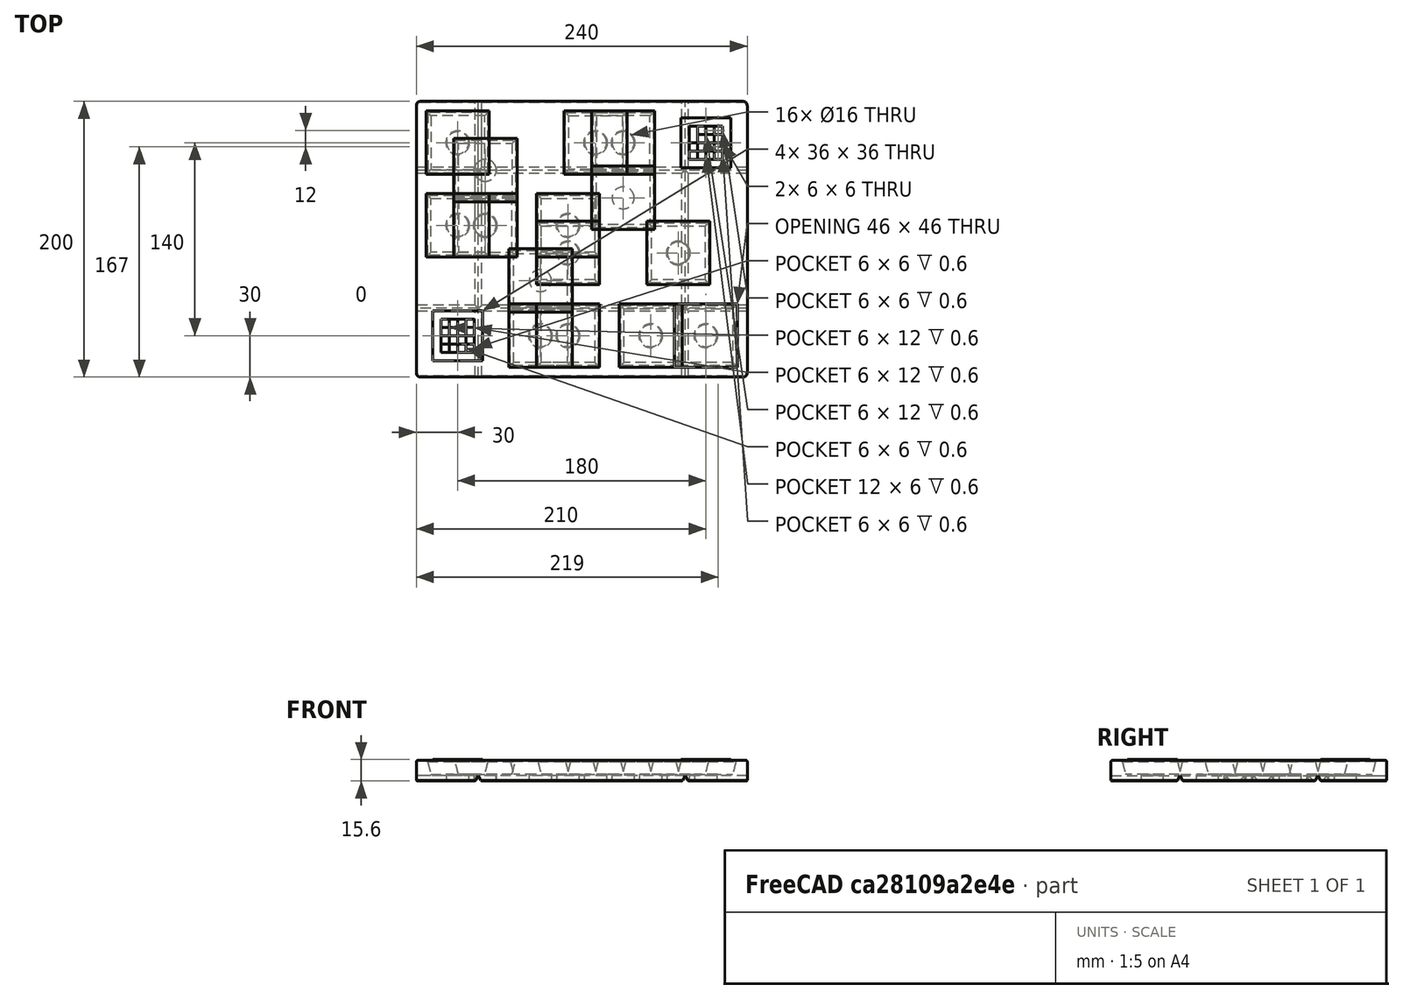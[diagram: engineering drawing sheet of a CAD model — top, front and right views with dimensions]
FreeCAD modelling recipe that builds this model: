
FCSTD DOCUMENT  (FreeCAD 0.21R33771 (Git))
Label: rob2024_plates
License: All rights reserved
LicenseURL: https://en.wikipedia.org/wiki/All_rights_reserved
objects: Sketcher::SketchObject×52, TechDraw::DrawViewDimension×44, PartDesign::SubtractiveLoft×16, PartDesign::Pocket×12, PartDesign::Chamfer×10, PartDesign::Pad×8, TechDraw::DrawGeomHatch×7, TechDraw::DrawSVGTemplate×4, PartDesign::Plane×4, PartDesign::Fillet×4, PartDesign::Body×4, TechDraw::DrawProjGroupItem×4, TechDraw::DrawProjGroup×4, TechDraw::DrawPage×4
note: 245 computed .brp shape members not serialized (recipe doc carries the construction recipe); baked Part::Feature solids carry a one-line shape summary decoded from their .brp

FEATURE [TechDraw::DrawSVGTemplate] Template
  Height = 297
  Orientation = 0
  Template = C:/Program Files/FreeCAD 0.21/data/Mod/TechDraw/Templates/A4_Portrait_blank.svg
  Width = 210
FEATURE [Sketcher::SketchObject] Sketch015
  FullyConstrained = true
  MapMode = 5
  Support = -> [XY_Plane001]
  sketch-geometry (16):
    g0: LineSegment StartX=-27 StartY=170 StartZ=0 EndX=207 EndY=170 EndZ=0
    g1: LineSegment StartX=210 StartY=167 StartZ=0 EndX=210 EndY=-27 EndZ=0
    g2: LineSegment StartX=207 StartY=-30 StartZ=0 EndX=-27 EndY=-30 EndZ=0
    g3: LineSegment StartX=-30 StartY=-27 StartZ=0 EndX=-30 EndY=167 EndZ=0
    g4: LineSegment StartX=-25 StartY=25 StartZ=0 EndX=25 EndY=25 EndZ=0
    g5: LineSegment StartX=25 StartY=25 StartZ=0 EndX=25 EndY=-25 EndZ=0
    g6: LineSegment StartX=25 StartY=-25 StartZ=0 EndX=-25 EndY=-25 EndZ=0
    g7: LineSegment StartX=-25 StartY=-25 StartZ=0 EndX=-25 EndY=25 EndZ=0
    g8: LineSegment StartX=155 StartY=165 StartZ=0 EndX=205 EndY=165 EndZ=0
    g9: LineSegment StartX=205 StartY=165 StartZ=0 EndX=205 EndY=115 EndZ=0
    g10: LineSegment StartX=205 StartY=115 StartZ=0 EndX=155 EndY=115 EndZ=0
    g11: LineSegment StartX=155 StartY=115 StartZ=0 EndX=155 EndY=165 EndZ=0
    g12: ArcOfCircle CenterX=-27 CenterY=-27 CenterZ=0 NormalX=0 NormalY=0 NormalZ=1 AngleXU=0 Radius=3 StartAngle=3.14159 EndAngle=4.71239
    g13: ArcOfCircle CenterX=207 CenterY=-27 CenterZ=0 NormalX=0 NormalY=0 NormalZ=1 AngleXU=0 Radius=3 StartAngle=4.71239 EndAngle=6.28319
    g14: ArcOfCircle CenterX=207 CenterY=167 CenterZ=0 NormalX=0 NormalY=0 NormalZ=1 AngleXU=0 Radius=3 StartAngle=1.7e-15 EndAngle=1.5708
    g15: ArcOfCircle CenterX=-27 CenterY=167 CenterZ=0 NormalX=0 NormalY=0 NormalZ=1 AngleXU=0 Radius=3 StartAngle=1.5708 EndAngle=3.14159
  constraints (44):
    c: Horizontal(g0)
    c: Horizontal(g2)
    c: Vertical(g1)
    c: Vertical(g3)
    c: Coincident(g4,g5)
    c: Coincident(g5,g6)
    c: Coincident(g6,g7)
    c: Coincident(g7,g4)
    c: Horizontal(g4)
    c: Horizontal(g6)
    c: Vertical(g5)
    c: Vertical(g7)
    c: DistanceY(g7,g7) = 50
    c: Coincident(g8,g9)
    c: Coincident(g9,g10)
    c: Coincident(g10,g11)
    c: Coincident(g11,g8)
    c: Horizontal(g8)
    c: Horizontal(g10)
    c: Vertical(g9)
    c: Vertical(g11)
    c: DistanceY(g9,g9) = 50
    c: DistanceX(g10,g10) = 50
    c: Distance(g9,g1) = 5
    c: Distance(g4,g3) = 5
    c: Distance(g6,g2) = 5
    c: Distance(g8,g0) = 5
    c: DistanceX(g6,g6) = 50
    c: Tangent(g2,g12) = 1.5708
    c: Tangent(g3,g12) = 1.5708
    c: Radius(g12) = 3
    c: Distance(g2,g0) = 200
    c: Tangent(g2,g13) = 1.5708
    c: Tangent(g1,g13) = 1.5708
    c: Tangent(g0,g14) = 1.5708
    c: Tangent(g1,g14) = 1.5708
    c: Tangent(g0,g15) = 1.5708
    c: Tangent(g3,g15) = 1.5708
    c: Equal(g12,g15)
    c: Equal(g12,g14)
    c: Equal(g12,g13)
    c: Distance(g3,g-2) = 30
    c: Distance(g2,g-1) = 30
    c: Distance(g3,g1) = 240
FEATURE [PartDesign::Pad] Pad002
  Direction = (0,0,1)
  Length = 15
  Length2 = 10
  Profile = -> Sketch015
  ReferenceAxis = -> Sketch015 [N_Axis]
  Reversed = true
  Type = 0
FEATURE [Sketcher::SketchObject] Sketch016  label="Sketch_rails_short_02"
  ExternalGeometry = -> [Pad002]
  FullyConstrained = true
  MapMode = 5
  Placement = pos=(210,0,0) rot=(0.57735,0.57735,0.57735;2.0944rad)
  Support = -> [Pad002]
  sketch-geometry (6):
    g0: LineSegment StartX=17.6906 StartY=-15 StartZ=0 EndX=20 EndY=-11 EndZ=0
    g1: LineSegment StartX=20 StartY=-11 StartZ=0 EndX=22.3094 EndY=-15 EndZ=0
    g2: LineSegment StartX=22.3094 StartY=-15 StartZ=0 EndX=17.6906 EndY=-15 EndZ=0
    g3: LineSegment StartX=117.691 StartY=-15 StartZ=0 EndX=120 EndY=-11 EndZ=0
    g4: LineSegment StartX=120 StartY=-11 StartZ=0 EndX=122.309 EndY=-15 EndZ=0
    g5: LineSegment StartX=122.309 StartY=-15 StartZ=0 EndX=117.691 EndY=-15 EndZ=0
  constraints (18):
    c: PointOnObject(g0,g-4)
    c: Coincident(g1,g0)
    c: PointOnObject(g1,g-4)
    c: Coincident(g2,g1)
    c: Coincident(g2,g0)
    c: Distance(g0,g2) = 4
    c: Angle(g0,g-2) = 0.523599
    c: Angle(g-2,g1) = 0.523599
    c: Coincident(g4,g3)
    c: Coincident(g5,g4)
    c: Coincident(g5,g3)
    c: Distance(g3,g5) = 4
    c: Angle(g3,g-2) = 0.523599
    c: Angle(g-2,g4) = 0.523599
    c: PointOnObject(g3,g-4)
    c: PointOnObject(g4,g-4)
    c: Distance(g0,g3) = 100
    c: Distance(g0,g-3) = 50
FEATURE [PartDesign::Pocket] Pocket003
  BaseFeature = -> Pad002
  Direction = (-1,0,0)
  Length = 5
  Length2 = 5
  Profile = -> Sketch016
  ReferenceAxis = -> Sketch016 [N_Axis]
  Type = 1
FEATURE [Sketcher::SketchObject] Sketch017  label="Sketch_rails_long_02"
  ExternalGeometry = -> [Pocket003]
  FullyConstrained = true
  MapMode = 5
  Placement = pos=(0,-30,0) rot=(1,0,0;1.5708rad)
  Support = -> [Pocket003]
  sketch-geometry (7):
    g0: LineSegment StartX=12.6906 StartY=-15 StartZ=0 EndX=15 EndY=-11 EndZ=0
    g1: LineSegment StartX=15 StartY=-11 StartZ=0 EndX=17.3094 EndY=-15 EndZ=0
    g2: LineSegment StartX=17.3094 StartY=-15 StartZ=0 EndX=12.6906 EndY=-15 EndZ=0
    g3: LineSegment StartX=162.691 StartY=-15 StartZ=0 EndX=165 EndY=-11 EndZ=0
    g4: LineSegment StartX=165 StartY=-11 StartZ=0 EndX=167.309 EndY=-15 EndZ=0
    g5: LineSegment StartX=167.309 StartY=-15 StartZ=0 EndX=162.691 EndY=-15 EndZ=0
    g6: LineSegment StartX=-30 StartY=-11 StartZ=0 EndX=210 EndY=-11 EndZ=0
  constraints (22):
    c: PointOnObject(g0,g-4)
    c: Coincident(g1,g0)
    c: PointOnObject(g1,g-4)
    c: Coincident(g2,g0)
    c: PointOnObject(g3,g-4)
    c: PointOnObject(g4,g-4)
    c: Coincident(g5,g3)
    c: Horizontal(g6)
    c: Distance(g-4,g6) = 4
    c: PointOnObject(g0,g6)
    c: PointOnObject(g3,g6)
    c: Coincident(g4,g3)
    c: DistanceX(g6,g6) = 240
    c: PointOnObject(g6,g-3)
    c: Angle(g0,g-2) = 0.523599
    c: Angle(g-2,g1) = 0.523599
    c: Angle(g3,g-2) = 0.523599
    c: Angle(g-2,g4) = 0.523599
    c: Coincident(g2,g1)
    c: Coincident(g5,g4)
    c: Distance(g0,g3) = 150
    c: Distance(g0,g-3) = 45
FEATURE [PartDesign::Pocket] Pocket004
  BaseFeature = -> Pocket003
  Direction = (0,1,-2e-16)
  Length = 5
  Length2 = 5
  Profile = -> Sketch017
  ReferenceAxis = -> Sketch017 [N_Axis]
  Type = 1
FEATURE [Sketcher::SketchObject] Sketch018
  ExternalGeometry = -> [Pocket004]
  FullyConstrained = true
  MapMode = 5
  Support = -> [Pocket004]
  sketch-geometry (42):
    g0: LineSegment StartX=-18 StartY=18 StartZ=0 EndX=18 EndY=18 EndZ=0
    g1: LineSegment StartX=18 StartY=18 StartZ=0 EndX=18 EndY=-18 EndZ=0
    g2: LineSegment StartX=18 StartY=-18 StartZ=0 EndX=-18 EndY=-18 EndZ=0
    g3: LineSegment StartX=-18 StartY=-18 StartZ=0 EndX=-18 EndY=18 EndZ=0
    g4: LineSegment StartX=180 StartY=170 StartZ=0 EndX=180 EndY=-30 EndZ=0
    g5: LineSegment StartX=-30 StartY=140 StartZ=0 EndX=210 EndY=140 EndZ=0
    g6: LineSegment StartX=162 StartY=158 StartZ=0 EndX=198 EndY=158 EndZ=0
    g7: LineSegment StartX=198 StartY=158 StartZ=0 EndX=198 EndY=122 EndZ=0
    g8: LineSegment StartX=198 StartY=122 StartZ=0 EndX=162 EndY=122 EndZ=0
    g9: LineSegment StartX=162 StartY=122 StartZ=0 EndX=162 EndY=158 EndZ=0
    g10: LineSegment StartX=-12 StartY=12 StartZ=0 EndX=-12 EndY=0 EndZ=0
    g11: LineSegment StartX=-12 StartY=0 StartZ=0 EndX=-6 EndY=0 EndZ=0
    g12: LineSegment StartX=-6 StartY=0 StartZ=0 EndX=-6 EndY=-12 EndZ=0
    g13: LineSegment StartX=-6 StartY=-12 StartZ=0 EndX=6 EndY=-12 EndZ=0
    g14: LineSegment StartX=6 StartY=-12 StartZ=0 EndX=6 EndY=-6 EndZ=0
    g15: LineSegment StartX=6 StartY=-6 StartZ=0 EndX=0 EndY=-6 EndZ=0
    g16: LineSegment StartX=0 StartY=0 StartZ=0 EndX=-6 EndY=1e-16 EndZ=0
    g17: LineSegment StartX=-6 StartY=1e-16 StartZ=0 EndX=-6 EndY=12 EndZ=0
    g18: LineSegment StartX=-6 StartY=12 StartZ=0 EndX=-12 EndY=12 EndZ=0
    g19: LineSegment StartX=6 StartY=12 StartZ=0 EndX=6 EndY=0 EndZ=0
    g20: LineSegment StartX=6 StartY=0 StartZ=0 EndX=12 EndY=1e-16 EndZ=0
    g21: LineSegment StartX=12 StartY=1e-16 StartZ=0 EndX=12 EndY=12 EndZ=0
    g22: LineSegment StartX=12 StartY=12 StartZ=0 EndX=6 EndY=12 EndZ=0
    g23: LineSegment StartX=0 StartY=-6 StartZ=0 EndX=0 EndY=0 EndZ=0
    g24: LineSegment StartX=168 StartY=128 StartZ=0 EndX=186 EndY=128 EndZ=0
    g25: LineSegment StartX=186 StartY=128 StartZ=0 EndX=186 EndY=134 EndZ=0
    g26: LineSegment StartX=186 StartY=134 StartZ=0 EndX=192 EndY=134 EndZ=0
    g27: LineSegment StartX=192 StartY=134 StartZ=0 EndX=192 EndY=140 EndZ=0
    g28: LineSegment StartX=192 StartY=140 StartZ=0 EndX=186 EndY=140 EndZ=0
    g29: LineSegment StartX=186 StartY=140 StartZ=0 EndX=186 EndY=134 EndZ=0
    g30: LineSegment StartX=186 StartY=134 StartZ=0 EndX=174 EndY=134 EndZ=0
    g31: LineSegment StartX=174 StartY=134 StartZ=0 EndX=174 EndY=140 EndZ=0
    g32: LineSegment StartX=174 StartY=140 StartZ=0 EndX=180 EndY=140 EndZ=0
    g33: LineSegment StartX=180 StartY=140 StartZ=0 EndX=180 EndY=152 EndZ=0
    g34: LineSegment StartX=180 StartY=152 StartZ=0 EndX=174 EndY=152 EndZ=0
    g35: LineSegment StartX=174 StartY=152 StartZ=0 EndX=174 EndY=140 EndZ=0
    g36: LineSegment StartX=174 StartY=140 StartZ=0 EndX=168 EndY=140 EndZ=0
    g37: LineSegment StartX=168 StartY=140 StartZ=0 EndX=168 EndY=128 EndZ=0
    g38: LineSegment StartX=186 StartY=152 StartZ=0 EndX=186 EndY=146 EndZ=0
    g39: LineSegment StartX=186 StartY=146 StartZ=0 EndX=192 EndY=146 EndZ=0
    g40: LineSegment StartX=192 StartY=146 StartZ=0 EndX=192 EndY=152 EndZ=0
    g41: LineSegment StartX=192 StartY=152 StartZ=0 EndX=186 EndY=152 EndZ=0
  constraints (113):
    c: Coincident(g0,g1)
    c: Coincident(g1,g2)
    c: Coincident(g2,g3)
    c: Coincident(g3,g0)
    c: Horizontal(g0)
    c: Vertical(g1)
    c: DistanceX(g2,g2) = 36
    c: Equal(g2,g1)
    c: Symmetric(g2,g1,g-2)
    c: Symmetric(g0,g2,g-1)
    c: Vertical(g4)
    c: Horizontal(g5)
    c: PointOnObject(g4,g-5)
    c: PointOnObject(g4,g-4)
    c: PointOnObject(g5,g-6)
    c: PointOnObject(g5,g-3)
    c: Distance(g5,g-1) = 140
    c: Distance(g4,g-2) = 180
    c: Coincident(g6,g7)
    c: Coincident(g7,g8)
    c: Coincident(g8,g9)
    c: Coincident(g9,g6)
    c: Horizontal(g6)
    c: Horizontal(g8)
    c: Vertical(g7)
    c: Vertical(g9)
    c: DistanceY(g7,g7) = 36
    c: Equal(g6,g7)
    c: Distance(g6,g5) = 18
    c: Distance(g6,g4) = 18
    c: Vertical(g10)
    c: Horizontal(g11)
    c: Vertical(g12)
    c: Coincident(g12,g13)
    c: Horizontal(g13)
    c: Vertical(g14)
    c: Coincident(g14,g15)
    c: Horizontal(g15)
    c: Coincident(g16,g17)
    c: Coincident(g18,g10)
    c: Horizontal(g18)
    c: Coincident(g19,g20)
    c: Vertical(g21)
    c: Coincident(g21,g22)
    c: Coincident(g22,g19)
    c: Coincident(g11,g10)
    c: Distance(g10,g3) = 6
    c: Distance(g12,g10) = 6
    c: Distance(g15,g12) = 6
    c: Distance(g15,g14) = 6
    c: Coincident(g11,g12)
    c: Coincident(g13,g14)
    c: Tangent(g11,g16)
    c: Coincident(g18,g17)
    c: Tangent(g19,g14)
    c: Coincident(g20,g21)
    c: DistanceX(g20,g20) = 6
    c: Tangent(g18,g22)
    c: Coincident(g23,g15)
    c: Coincident(g23,g16)
    c: Vertical(g23)
    c: Tangent(g11,g20)
    c: Tangent(g17,g12)
    c: Distance(g12,g2) = 6
    c: Distance(g15,g13) = 6
    c: Distance(g16,g15) = 6
    c: Distance(g17,g11) = 12
    c: Horizontal(g24)
    c: Coincident(g25,g24)
    c: Vertical(g25)
    c: Horizontal(g26)
    c: Vertical(g27)
    c: Horizontal(g28)
    c: Vertical(g31)
    c: Vertical(g33)
    c: Coincident(g34,g33)
    c: Horizontal(g34)
    c: Vertical(g37)
    c: Coincident(g24,g37)
    c: Coincident(g37,g36)
    c: Coincident(g39,g38)
    c: Horizontal(g39)
    c: Coincident(g41,g38)
    c: Distance(g24,g9) = 6
    c: Distance(g30,g37) = 6
    c: Distance(g32,g31) = 6
    c: Coincident(g31,g30)
    c: Coincident(g32,g31)
    c: Coincident(g33,g32)
    c: Tangent(g35,g31)
    c: Coincident(g34,g35)
    c: Coincident(g36,g35)
    c: Distance(g28,g33) = 6
    c: Coincident(g29,g30)
    c: Coincident(g29,g28)
    c: Tangent(g29,g25)
    c: Coincident(g26,g25)
    c: Distance(g27,g29) = 6
    c: Coincident(g28,g27)
    c: Coincident(g26,g27)
    c: Tangent(g41,g34)
    c: Tangent(g38,g29)
    c: Tangent(g40,g27)
    c: Coincident(g41,g40)
    c: Coincident(g39,g40)
    c: Tangent(g36,g32)
    c: Tangent(g30,g26)
    c: Tangent(g28,g32)
    c: Distance(g39,g28) = 6
    c: Distance(g40,g39) = 6
    c: Distance(g27,g26) = 6
    c: Distance(g26,g24) = 6
    c: Distance(g24,g8) = 6
FEATURE [PartDesign::Pad] Pad003
  BaseFeature = -> Pocket004
  Direction = (0,0,1)
  Length = 0.6
  Length2 = 10
  Profile = -> Sketch018
  ReferenceAxis = -> Sketch018 [N_Axis]
  Type = 0
FEATURE [Sketcher::SketchObject] Sketch019
  FullyConstrained = true
  MapMode = 5
  Support = -> [Pad003]
  sketch-geometry (4):
    g0: Circle CenterX=20 CenterY=120 CenterZ=0 NormalX=0 NormalY=0 NormalZ=1 AngleXU=0 Radius=8
    g1: Circle CenterX=120 CenterY=100 CenterZ=0 NormalX=0 NormalY=0 NormalZ=1 AngleXU=0 Radius=8
    g2: Circle CenterX=180 CenterY=0 CenterZ=0 NormalX=0 NormalY=0 NormalZ=1 AngleXU=0 Radius=8
    g3: Circle CenterX=60 CenterY=40 CenterZ=0 NormalX=0 NormalY=0 NormalZ=1 AngleXU=0 Radius=8
  constraints (12):
    c: Diameter(g0) = 16
    c: PointOnObject(g2,g-1)
    c: Distance(g2,g-2) = 180
    c: Equal(g2,g0)
    c: Distance(g3,g-1) = 40
    c: Distance(g3,g-2) = 60
    c: Equal(g3,g0)
    c: Distance(g1,g-2) = 120
    c: Distance(g1,g-1) = 100
    c: Equal(g0,g1)
    c: Distance(g0,g-1) = 120
    c: Distance(g0,g-2) = 20
FEATURE [PartDesign::Pocket] Pocket005
  BaseFeature = -> Pad003
  Direction = (0,0,-1)
  Length = 5
  Length2 = 5
  Profile = -> Sketch019
  ReferenceAxis = -> Sketch019 [N_Axis]
  Type = 1
FEATURE [PartDesign::Plane] DatumPlane001
  AttachmentOffset = pos=(0,0,-10) rot=(0,0,1;0rad)
  Length = 60
  MapMode = 5
  Placement = pos=(0,0,-10) rot=(0,0,1;0rad)
  ResizeMode = 0
  Support = -> [Pocket005]
  Width = 60
FEATURE [Sketcher::SketchObject] Sketch020
  ExternalGeometry = -> [Pocket005]
  FullyConstrained = true
  MapMode = 5
  Support = -> [Pocket005]
  sketch-geometry (4):
    g0: LineSegment StartX=38 StartY=62 StartZ=0 EndX=82 EndY=62 EndZ=0
    g1: LineSegment StartX=82 StartY=62 StartZ=0 EndX=82 EndY=18 EndZ=0
    g2: LineSegment StartX=82 StartY=18 StartZ=0 EndX=38 EndY=18 EndZ=0
    g3: LineSegment StartX=38 StartY=18 StartZ=0 EndX=38 EndY=62 EndZ=0
  constraints (11):
    c: Coincident(g0,g1)
    c: Coincident(g1,g2)
    c: Coincident(g2,g3)
    c: Coincident(g3,g0)
    c: Horizontal(g0)
    c: Horizontal(g2)
    c: Vertical(g1)
    c: Vertical(g3)
    c: DistanceY(g3,g3) = 44
    c: Equal(g3,g0)
    c: Symmetric(g0,g1,g-3)
FEATURE [Sketcher::SketchObject] Sketch021
  ExternalGeometry = -> [Pocket005]
  FullyConstrained = true
  MapMode = 5
  Placement = pos=(0,0,-10) rot=(0,0,1;0rad)
  Support = -> [DatumPlane001]
  sketch-geometry (4):
    g0: LineSegment StartX=40.5 StartY=59.5 StartZ=0 EndX=79.5 EndY=59.5 EndZ=0
    g1: LineSegment StartX=79.5 StartY=59.5 StartZ=0 EndX=79.5 EndY=20.5 EndZ=0
    g2: LineSegment StartX=79.5 StartY=20.5 StartZ=0 EndX=40.5 EndY=20.5 EndZ=0
    g3: LineSegment StartX=40.5 StartY=20.5 StartZ=0 EndX=40.5 EndY=59.5 EndZ=0
  constraints (11):
    c: Coincident(g0,g1)
    c: Coincident(g1,g2)
    c: Coincident(g2,g3)
    c: Coincident(g3,g0)
    c: Horizontal(g0)
    c: Horizontal(g2)
    c: Vertical(g1)
    c: Vertical(g3)
    c: DistanceY(g3,g3) = 39
    c: Equal(g3,g0)
    c: Symmetric(g0,g1,g-3)
FEATURE [Sketcher::SketchObject] Sketch022
  ExternalGeometry = -> [Pocket005]
  FullyConstrained = true
  MapMode = 5
  Support = -> [Pocket005]
  sketch-geometry (4):
    g0: LineSegment StartX=98 StartY=122 StartZ=0 EndX=142 EndY=122 EndZ=0
    g1: LineSegment StartX=142 StartY=122 StartZ=0 EndX=142 EndY=78 EndZ=0
    g2: LineSegment StartX=142 StartY=78 StartZ=0 EndX=98 EndY=78 EndZ=0
    g3: LineSegment StartX=98 StartY=78 StartZ=0 EndX=98 EndY=122 EndZ=0
  constraints (11):
    c: Coincident(g0,g1)
    c: Coincident(g1,g2)
    c: Coincident(g2,g3)
    c: Coincident(g3,g0)
    c: Horizontal(g0)
    c: Horizontal(g2)
    c: Vertical(g1)
    c: Vertical(g3)
    c: DistanceY(g3,g3) = 44
    c: Equal(g3,g0)
    c: Symmetric(g0,g1,g-3)
FEATURE [Sketcher::SketchObject] Sketch023
  ExternalGeometry = -> [Pocket005]
  FullyConstrained = true
  MapMode = 5
  Placement = pos=(0,0,-10) rot=(0,0,1;0rad)
  Support = -> [DatumPlane001]
  sketch-geometry (4):
    g0: LineSegment StartX=100.5 StartY=119.5 StartZ=0 EndX=139.5 EndY=119.5 EndZ=0
    g1: LineSegment StartX=139.5 StartY=119.5 StartZ=0 EndX=139.5 EndY=80.5 EndZ=0
    g2: LineSegment StartX=139.5 StartY=80.5 StartZ=0 EndX=100.5 EndY=80.5 EndZ=0
    g3: LineSegment StartX=100.5 StartY=80.5 StartZ=0 EndX=100.5 EndY=119.5 EndZ=0
  constraints (11):
    c: Coincident(g0,g1)
    c: Coincident(g1,g2)
    c: Coincident(g2,g3)
    c: Coincident(g3,g0)
    c: Horizontal(g0)
    c: Horizontal(g2)
    c: Vertical(g1)
    c: Vertical(g3)
    c: DistanceY(g3,g3) = 39
    c: Equal(g3,g0)
    c: Symmetric(g0,g1,g-3)
FEATURE [Sketcher::SketchObject] Sketch026
  ExternalGeometry = -> [Pocket005]
  FullyConstrained = true
  MapMode = 5
  Support = -> [Pocket005]
  sketch-geometry (4):
    g0: LineSegment StartX=-2 StartY=142 StartZ=0 EndX=42 EndY=142 EndZ=0
    g1: LineSegment StartX=42 StartY=142 StartZ=0 EndX=42 EndY=98 EndZ=0
    g2: LineSegment StartX=42 StartY=98 StartZ=0 EndX=-2 EndY=98 EndZ=0
    g3: LineSegment StartX=-2 StartY=98 StartZ=0 EndX=-2 EndY=142 EndZ=0
  constraints (11):
    c: Coincident(g0,g1)
    c: Coincident(g1,g2)
    c: Coincident(g2,g3)
    c: Coincident(g3,g0)
    c: Horizontal(g0)
    c: Horizontal(g2)
    c: Vertical(g1)
    c: Vertical(g3)
    c: DistanceY(g3,g3) = 44
    c: Equal(g3,g0)
    c: Symmetric(g0,g1,g-3)
FEATURE [Sketcher::SketchObject] Sketch027
  ExternalGeometry = -> [Pocket005]
  FullyConstrained = true
  MapMode = 5
  Placement = pos=(0,0,-10) rot=(0,0,1;0rad)
  Support = -> [DatumPlane001]
  sketch-geometry (4):
    g0: LineSegment StartX=0.5 StartY=139.5 StartZ=0 EndX=39.5 EndY=139.5 EndZ=0
    g1: LineSegment StartX=39.5 StartY=139.5 StartZ=0 EndX=39.5 EndY=100.5 EndZ=0
    g2: LineSegment StartX=39.5 StartY=100.5 StartZ=0 EndX=0.5 EndY=100.5 EndZ=0
    g3: LineSegment StartX=0.5 StartY=100.5 StartZ=0 EndX=0.5 EndY=139.5 EndZ=0
  constraints (11):
    c: Coincident(g0,g1)
    c: Coincident(g1,g2)
    c: Coincident(g2,g3)
    c: Coincident(g3,g0)
    c: Horizontal(g0)
    c: Horizontal(g2)
    c: Vertical(g1)
    c: Vertical(g3)
    c: DistanceY(g3,g3) = 39
    c: Equal(g0,g3)
    c: Symmetric(g0,g1,g-3)
FEATURE [PartDesign::SubtractiveLoft] SubtractiveLoft004
  BaseFeature = -> Pocket005
  Closed = false
  Profile = -> Sketch027
  Ruled = false
  Sections = -> [Sketch026]
FEATURE [PartDesign::SubtractiveLoft] SubtractiveLoft005
  BaseFeature = -> SubtractiveLoft004
  Closed = false
  Profile = -> Sketch020
  Ruled = false
  Sections = -> [Sketch021]
FEATURE [PartDesign::SubtractiveLoft] SubtractiveLoft006
  BaseFeature = -> SubtractiveLoft005
  Closed = false
  Profile = -> Sketch022
  Ruled = false
  Sections = -> [Sketch023]
FEATURE [Sketcher::SketchObject] Sketch024
  ExternalGeometry = -> [SubtractiveLoft006]
  FullyConstrained = true
  MapMode = 5
  Support = -> [SubtractiveLoft006]
  sketch-geometry (4):
    g0: LineSegment StartX=158 StartY=22 StartZ=0 EndX=202 EndY=22 EndZ=0
    g1: LineSegment StartX=202 StartY=22 StartZ=0 EndX=202 EndY=-22 EndZ=0
    g2: LineSegment StartX=202 StartY=-22 StartZ=0 EndX=158 EndY=-22 EndZ=0
    g3: LineSegment StartX=158 StartY=-22 StartZ=0 EndX=158 EndY=22 EndZ=0
  constraints (11):
    c: Coincident(g0,g1)
    c: Coincident(g1,g2)
    c: Coincident(g2,g3)
    c: Coincident(g3,g0)
    c: Horizontal(g0)
    c: Horizontal(g2)
    c: Vertical(g1)
    c: Vertical(g3)
    c: DistanceY(g3,g3) = 44
    c: Equal(g3,g0)
    c: Symmetric(g0,g1,g-3)
FEATURE [Sketcher::SketchObject] Sketch025
  ExternalGeometry = -> [SubtractiveLoft006]
  FullyConstrained = true
  MapMode = 5
  Placement = pos=(0,0,-10) rot=(0,0,1;0rad)
  Support = -> [DatumPlane001]
  sketch-geometry (4):
    g0: LineSegment StartX=160.5 StartY=19.5 StartZ=0 EndX=199.5 EndY=19.5 EndZ=0
    g1: LineSegment StartX=199.5 StartY=19.5 StartZ=0 EndX=199.5 EndY=-19.5 EndZ=0
    g2: LineSegment StartX=199.5 StartY=-19.5 StartZ=0 EndX=160.5 EndY=-19.5 EndZ=0
    g3: LineSegment StartX=160.5 StartY=-19.5 StartZ=0 EndX=160.5 EndY=19.5 EndZ=0
  constraints (11):
    c: Coincident(g0,g1)
    c: Coincident(g1,g2)
    c: Coincident(g2,g3)
    c: Coincident(g3,g0)
    c: Horizontal(g0)
    c: Horizontal(g2)
    c: Vertical(g1)
    c: Vertical(g3)
    c: DistanceY(g3,g3) = 39
    c: Equal(g3,g0)
    c: Symmetric(g0,g1,g-3)
FEATURE [PartDesign::SubtractiveLoft] SubtractiveLoft007
  BaseFeature = -> SubtractiveLoft006
  Closed = false
  Profile = -> Sketch024
  Ruled = false
  Sections = -> [Sketch025]
FEATURE [PartDesign::Chamfer] Chamfer002
  Angle = 45
  Base = -> SubtractiveLoft007 [Edge30,Edge32,Edge33,Edge31,Edge22,Edge24,Edge23,Edge25,Edge37,Edge36,Edge34,Edge35,Edge29,Edge28,Edge26,Edge27]
  BaseFeature = -> SubtractiveLoft007
  ChamferType = 0
  FlipDirection = false
  Size = 1
  Size2 = 1
  SupportTransform = false
  UseAllEdges = false
FEATURE [PartDesign::Fillet] Fillet001
  Base = -> Chamfer002 [Edge9]
  BaseFeature = -> Chamfer002
  Radius = 1
  SupportTransform = false
  UseAllEdges = false
FEATURE [Sketcher::SketchObject] Sketch
  FullyConstrained = true
  MapMode = 5
  Support = -> [XY_Plane]
  sketch-geometry (16):
    g0: LineSegment StartX=-27 StartY=170 StartZ=0 EndX=207 EndY=170 EndZ=0
    g1: LineSegment StartX=210 StartY=167 StartZ=0 EndX=210 EndY=-27 EndZ=0
    g2: LineSegment StartX=207 StartY=-30 StartZ=0 EndX=-27 EndY=-30 EndZ=0
    g3: LineSegment StartX=-30 StartY=-27 StartZ=0 EndX=-30 EndY=167 EndZ=0
    g4: LineSegment StartX=-25 StartY=25 StartZ=0 EndX=25 EndY=25 EndZ=0
    g5: LineSegment StartX=25 StartY=25 StartZ=0 EndX=25 EndY=-25 EndZ=0
    g6: LineSegment StartX=25 StartY=-25 StartZ=0 EndX=-25 EndY=-25 EndZ=0
    g7: LineSegment StartX=-25 StartY=-25 StartZ=0 EndX=-25 EndY=25 EndZ=0
    g8: LineSegment StartX=155 StartY=165 StartZ=0 EndX=205 EndY=165 EndZ=0
    g9: LineSegment StartX=205 StartY=165 StartZ=0 EndX=205 EndY=115 EndZ=0
    g10: LineSegment StartX=205 StartY=115 StartZ=0 EndX=155 EndY=115 EndZ=0
    g11: LineSegment StartX=155 StartY=115 StartZ=0 EndX=155 EndY=165 EndZ=0
    g12: ArcOfCircle CenterX=-27 CenterY=-27 CenterZ=0 NormalX=0 NormalY=0 NormalZ=1 AngleXU=0 Radius=3 StartAngle=3.14159 EndAngle=4.71239
    g13: ArcOfCircle CenterX=207 CenterY=-27 CenterZ=0 NormalX=0 NormalY=0 NormalZ=1 AngleXU=0 Radius=3 StartAngle=4.71239 EndAngle=6.28319
    g14: ArcOfCircle CenterX=207 CenterY=167 CenterZ=0 NormalX=0 NormalY=0 NormalZ=1 AngleXU=0 Radius=3 StartAngle=1.7e-15 EndAngle=1.5708
    g15: ArcOfCircle CenterX=-27 CenterY=167 CenterZ=0 NormalX=0 NormalY=0 NormalZ=1 AngleXU=0 Radius=3 StartAngle=1.5708 EndAngle=3.14159
  constraints (44):
    c: Horizontal(g0)
    c: Horizontal(g2)
    c: Vertical(g1)
    c: Vertical(g3)
    c: Coincident(g4,g5)
    c: Coincident(g5,g6)
    c: Coincident(g6,g7)
    c: Coincident(g7,g4)
    c: Horizontal(g4)
    c: Horizontal(g6)
    c: Vertical(g5)
    c: Vertical(g7)
    c: DistanceY(g7,g7) = 50
    c: Coincident(g8,g9)
    c: Coincident(g9,g10)
    c: Coincident(g10,g11)
    c: Coincident(g11,g8)
    c: Horizontal(g8)
    c: Horizontal(g10)
    c: Vertical(g9)
    c: Vertical(g11)
    c: DistanceY(g9,g9) = 50
    c: DistanceX(g10,g10) = 50
    c: Distance(g9,g1) = 5
    c: Distance(g4,g3) = 5
    c: Distance(g6,g2) = 5
    c: Distance(g8,g0) = 5
    c: DistanceX(g6,g6) = 50
    c: Tangent(g2,g12) = 1.5708
    c: Tangent(g3,g12) = 1.5708
    c: Radius(g12) = 3
    c: Distance(g2,g0) = 200
    c: Tangent(g2,g13) = 1.5708
    c: Tangent(g1,g13) = 1.5708
    c: Tangent(g0,g14) = 1.5708
    c: Tangent(g1,g14) = 1.5708
    c: Tangent(g0,g15) = 1.5708
    c: Tangent(g3,g15) = 1.5708
    c: Equal(g12,g15)
    c: Equal(g12,g14)
    c: Equal(g12,g13)
    c: Distance(g3,g-2) = 30
    c: Distance(g2,g-1) = 30
    c: Distance(g3,g1) = 240
FEATURE [PartDesign::Pad] Pad
  Direction = (0,0,1)
  Length = 15
  Length2 = 10
  Profile = -> Sketch
  ReferenceAxis = -> Sketch [N_Axis]
  Reversed = true
  Type = 0
FEATURE [Sketcher::SketchObject] Sketch001  label="Sketch_rails_short"
  ExternalGeometry = -> [Pad]
  FullyConstrained = true
  MapMode = 5
  Placement = pos=(210,0,0) rot=(0.57735,0.57735,0.57735;2.0944rad)
  Support = -> [Pad]
  sketch-geometry (6):
    g0: LineSegment StartX=17.6906 StartY=-15 StartZ=0 EndX=20 EndY=-11 EndZ=0
    g1: LineSegment StartX=20 StartY=-11 StartZ=0 EndX=22.3094 EndY=-15 EndZ=0
    g2: LineSegment StartX=22.3094 StartY=-15 StartZ=0 EndX=17.6906 EndY=-15 EndZ=0
    g3: LineSegment StartX=117.691 StartY=-15 StartZ=0 EndX=120 EndY=-11 EndZ=0
    g4: LineSegment StartX=120 StartY=-11 StartZ=0 EndX=122.309 EndY=-15 EndZ=0
    g5: LineSegment StartX=122.309 StartY=-15 StartZ=0 EndX=117.691 EndY=-15 EndZ=0
  constraints (18):
    c: PointOnObject(g0,g-4)
    c: Coincident(g1,g0)
    c: PointOnObject(g1,g-4)
    c: Coincident(g2,g1)
    c: Coincident(g2,g0)
    c: Distance(g0,g2) = 4
    c: Angle(g0,g-2) = 0.523599
    c: Angle(g-2,g1) = 0.523599
    c: Coincident(g4,g3)
    c: Coincident(g5,g4)
    c: Coincident(g5,g3)
    c: Distance(g3,g5) = 4
    c: Angle(g3,g-2) = 0.523599
    c: Angle(g-2,g4) = 0.523599
    c: PointOnObject(g3,g-4)
    c: PointOnObject(g4,g-4)
    c: Distance(g0,g3) = 100
    c: Distance(g0,g-3) = 50
FEATURE [PartDesign::Pocket] Pocket
  BaseFeature = -> Pad
  Direction = (-1,0,0)
  Length = 5
  Length2 = 5
  Profile = -> Sketch001
  ReferenceAxis = -> Sketch001 [N_Axis]
  Type = 1
FEATURE [Sketcher::SketchObject] Sketch002
  ExternalGeometry = -> [Pocket]
  FullyConstrained = true
  MapMode = 5
  Placement = pos=(0,-30,0) rot=(1,0,0;1.5708rad)
  Support = -> [Pocket]
  sketch-geometry (7):
    g0: LineSegment StartX=12.6906 StartY=-15 StartZ=0 EndX=15 EndY=-11 EndZ=0
    g1: LineSegment StartX=15 StartY=-11 StartZ=0 EndX=17.3094 EndY=-15 EndZ=0
    g2: LineSegment StartX=17.3094 StartY=-15 StartZ=0 EndX=12.6906 EndY=-15 EndZ=0
    g3: LineSegment StartX=162.691 StartY=-15 StartZ=0 EndX=165 EndY=-11 EndZ=0
    g4: LineSegment StartX=165 StartY=-11 StartZ=0 EndX=167.309 EndY=-15 EndZ=0
    g5: LineSegment StartX=167.309 StartY=-15 StartZ=0 EndX=162.691 EndY=-15 EndZ=0
    g6: LineSegment StartX=-30 StartY=-11 StartZ=0 EndX=210 EndY=-11 EndZ=0
  constraints (22):
    c: PointOnObject(g0,g-4)
    c: Coincident(g1,g0)
    c: PointOnObject(g1,g-4)
    c: Coincident(g2,g0)
    c: PointOnObject(g3,g-4)
    c: PointOnObject(g4,g-4)
    c: Coincident(g5,g3)
    c: Horizontal(g6)
    c: Distance(g-4,g6) = 4
    c: PointOnObject(g0,g6)
    c: PointOnObject(g3,g6)
    c: Coincident(g4,g3)
    c: DistanceX(g6,g6) = 240
    c: PointOnObject(g6,g-3)
    c: Angle(g0,g-2) = 0.523599
    c: Angle(g-2,g1) = 0.523599
    c: Angle(g3,g-2) = 0.523599
    c: Angle(g-2,g4) = 0.523599
    c: Coincident(g2,g1)
    c: Coincident(g5,g4)
    c: Distance(g0,g3) = 150
    c: Distance(g0,g-3) = 45
FEATURE [PartDesign::Pocket] Pocket001
  BaseFeature = -> Pocket
  Direction = (0,1,-2e-16)
  Length = 5
  Length2 = 5
  Profile = -> Sketch002
  ReferenceAxis = -> Sketch002 [N_Axis]
  Type = 1
FEATURE [Sketcher::SketchObject] Sketch003
  ExternalGeometry = -> [Pocket001]
  FullyConstrained = true
  MapMode = 5
  Support = -> [Pocket001]
  sketch-geometry (36):
    g0: LineSegment StartX=-18 StartY=18 StartZ=0 EndX=18 EndY=18 EndZ=0
    g1: LineSegment StartX=18 StartY=18 StartZ=0 EndX=18 EndY=-18 EndZ=0
    g2: LineSegment StartX=18 StartY=-18 StartZ=0 EndX=-18 EndY=-18 EndZ=0
    g3: LineSegment StartX=-18 StartY=-18 StartZ=0 EndX=-18 EndY=18 EndZ=0
    g4: LineSegment StartX=-12 StartY=-12 StartZ=0 EndX=-12 EndY=6 EndZ=0
    g5: LineSegment StartX=-12 StartY=6 StartZ=0 EndX=12 EndY=6 EndZ=0
    g6: LineSegment StartX=12 StartY=6 StartZ=0 EndX=12 EndY=-6 EndZ=0
    g7: LineSegment StartX=12 StartY=-6 StartZ=0 EndX=6 EndY=-6 EndZ=0
    g8: LineSegment StartX=6 StartY=-6 StartZ=0 EndX=6 EndY=-12 EndZ=0
    g9: LineSegment StartX=6 StartY=-12 StartZ=0 EndX=9e-16 EndY=-12 EndZ=0
    g10: LineSegment StartX=9e-16 StartY=-12 StartZ=0 EndX=9e-16 EndY=-6 EndZ=0
    g11: LineSegment StartX=9e-16 StartY=-6 StartZ=0 EndX=6 EndY=-6 EndZ=0
    g12: LineSegment StartX=6 StartY=-6 StartZ=0 EndX=6 EndY=9e-16 EndZ=0
    g13: LineSegment StartX=6 StartY=9e-16 StartZ=0 EndX=-6 EndY=9e-16 EndZ=0
    g14: LineSegment StartX=-6 StartY=9e-16 StartZ=0 EndX=-6 EndY=-12 EndZ=0
    g15: LineSegment StartX=-6 StartY=-12 StartZ=0 EndX=-12 EndY=-12 EndZ=0
    g16: LineSegment StartX=180 StartY=170 StartZ=0 EndX=180 EndY=-30 EndZ=0
    g17: LineSegment StartX=-30 StartY=140 StartZ=0 EndX=210 EndY=140 EndZ=0
    g18: LineSegment StartX=162 StartY=158 StartZ=0 EndX=198 EndY=158 EndZ=0
    g19: LineSegment StartX=198 StartY=158 StartZ=0 EndX=198 EndY=122 EndZ=0
    g20: LineSegment StartX=198 StartY=122 StartZ=0 EndX=162 EndY=122 EndZ=0
    g21: LineSegment StartX=162 StartY=122 StartZ=0 EndX=162 EndY=158 EndZ=0
    g22: LineSegment StartX=180 StartY=128 StartZ=0 EndX=168 EndY=128 EndZ=0
    g23: LineSegment StartX=168 StartY=128 StartZ=0 EndX=168 EndY=134 EndZ=0
    g24: LineSegment StartX=168 StartY=134 StartZ=0 EndX=180 EndY=134 EndZ=0
    g25: LineSegment StartX=180 StartY=134 StartZ=0 EndX=180 EndY=152 EndZ=0
    g26: LineSegment StartX=180 StartY=152 StartZ=0 EndX=192 EndY=152 EndZ=0
    g27: LineSegment StartX=192 StartY=152 StartZ=0 EndX=192 EndY=140 EndZ=0
    g28: LineSegment StartX=192 StartY=140 StartZ=0 EndX=186 EndY=140 EndZ=0
    g29: LineSegment StartX=186 StartY=140 StartZ=0 EndX=186 EndY=134 EndZ=0
    g30: LineSegment StartX=186 StartY=134 StartZ=0 EndX=192 EndY=134 EndZ=0
    g31: LineSegment StartX=192 StartY=134 StartZ=0 EndX=192 EndY=128 EndZ=0
    g32: LineSegment StartX=192 StartY=128 StartZ=0 EndX=186 EndY=128 EndZ=0
    g33: LineSegment StartX=186 StartY=128 StartZ=0 EndX=186 EndY=134 EndZ=0
    g34: LineSegment StartX=186 StartY=134 StartZ=0 EndX=180 EndY=134 EndZ=0
    g35: LineSegment StartX=180 StartY=134 StartZ=0 EndX=180 EndY=128 EndZ=0
  constraints (108):
    c: Coincident(g0,g1)
    c: Coincident(g1,g2)
    c: Coincident(g2,g3)
    c: Coincident(g3,g0)
    c: Horizontal(g0)
    c: Vertical(g1)
    c: DistanceX(g2,g2) = 36
    c: Equal(g2,g1)
    c: Symmetric(g2,g1,g-2)
    c: Symmetric(g0,g2,g-1)
    c: Vertical(g4)
    c: Coincident(g5,g6)
    c: Coincident(g6,g7)
    c: Coincident(g7,g8)
    c: Coincident(g8,g9)
    c: Coincident(g10,g11)
    c: Horizontal(g11)
    c: Coincident(g11,g12)
    c: Vertical(g12)
    c: Horizontal(g13)
    c: Coincident(g13,g14)
    c: Vertical(g14)
    c: Coincident(g15,g4)
    c: Horizontal(g15)
    c: Coincident(g15,g14)
    c: Coincident(g10,g9)
    c: Coincident(g13,g12)
    c: Coincident(g5,g4)
    c: Horizontal(g5)
    c: Horizontal(g7)
    c: Horizontal(g9)
    c: Vertical(g10)
    c: Vertical(g8)
    c: Vertical(g6)
    c: Distance(g4,g3) = 6
    c: DistanceX(g15,g15) = 6
    c: DistanceX(g7,g7) = 6
    c: DistanceX(g9,g9) = 6
    c: Equal(g9,g11)
    c: Distance(g14,g10) = 6
    c: Distance(g4,g2) = 6
    c: DistanceY(g10,g10) = 6
    c: Equal(g10,g8)
    c: DistanceY(g12,g12) = 6
    c: Distance(g13,g5) = 6
    c: Distance(g8,g2) = 6
    c: Vertical(g16)
    c: Horizontal(g17)
    c: PointOnObject(g16,g-5)
    c: PointOnObject(g16,g-4)
    c: PointOnObject(g17,g-6)
    c: PointOnObject(g17,g-3)
    c: Distance(g17,g-1) = 140
    c: Distance(g16,g-2) = 180
    c: Coincident(g18,g19)
    c: Coincident(g19,g20)
    c: Coincident(g20,g21)
    c: Coincident(g21,g18)
    c: Horizontal(g18)
    c: Horizontal(g20)
    c: Vertical(g19)
    c: Vertical(g21)
    c: DistanceY(g19,g19) = 36
    c: Equal(g18,g19)
    c: Distance(g18,g17) = 18
    c: Distance(g18,g16) = 18
    c: Horizontal(g22)
    c: Coincident(g22,g23)
    c: Coincident(g23,g24)
    c: Horizontal(g24)
    c: Coincident(g24,g25)
    c: Coincident(g25,g26)
    c: Horizontal(g26)
    c: Coincident(g26,g27)
    c: Vertical(g27)
    c: Horizontal(g28)
    c: Vertical(g29)
    c: Coincident(g29,g30)
    c: Coincident(g30,g31)
    c: Coincident(g31,g32)
    c: Horizontal(g32)
    c: Vertical(g33)
    c: Coincident(g33,g34)
    c: Coincident(g34,g35)
    c: Coincident(g35,g22)
    c: Vertical(g23)
    c: Vertical(g31)
    c: Horizontal(g30)
    c: Horizontal(g34)
    c: Vertical(g25)
    c: Vertical(g35)
    c: Distance(g22,g21) = 6
    c: DistanceX(g22,g22) = 12
    c: DistanceX(g32,g32) = 6
    c: DistanceX(g34,g34) = 6
    c: Equal(g32,g30)
    c: Equal(g22,g24)
    c: Equal(g32,g28)
    c: Coincident(g27,g28)
    c: Distance(g31,g20) = 6
    c: Coincident(g32,g33)
    c: Distance(g22,g20) = 6
    c: DistanceY(g31,g31) = 6
    c: DistanceY(g29,g29) = 6
    c: Coincident(g28,g29)
    c: DistanceY(g27,g27) = 12
    c: Equal(g31,g33)
    c: Equal(g31,g23)
FEATURE [PartDesign::Pad] Pad001
  BaseFeature = -> Pocket001
  Direction = (0,0,1)
  Length = 0.6
  Length2 = 10
  Profile = -> Sketch003
  ReferenceAxis = -> Sketch003 [N_Axis]
  Type = 0
FEATURE [Sketcher::SketchObject] Sketch004
  FullyConstrained = true
  MapMode = 5
  Support = -> [Pad001]
  sketch-geometry (4):
    g0: Circle CenterX=0 CenterY=80 CenterZ=0 NormalX=0 NormalY=0 NormalZ=1 AngleXU=0 Radius=8
    g1: Circle CenterX=100 CenterY=140 CenterZ=0 NormalX=0 NormalY=0 NormalZ=1 AngleXU=0 Radius=8
    g2: Circle CenterX=140 CenterY=0 CenterZ=0 NormalX=0 NormalY=0 NormalZ=1 AngleXU=0 Radius=8
    g3: Circle CenterX=80 CenterY=60 CenterZ=0 NormalX=0 NormalY=0 NormalZ=1 AngleXU=0 Radius=8
  constraints (12):
    c: PointOnObject(g0,g-2)
    c: Diameter(g0) = 16
    c: Distance(g0,g-1) = 80
    c: PointOnObject(g2,g-1)
    c: Distance(g2,g-2) = 140
    c: Equal(g2,g0)
    c: Distance(g3,g-1) = 60
    c: Distance(g3,g-2) = 80
    c: Equal(g3,g0)
    c: Distance(g1,g-2) = 100
    c: Distance(g1,g-1) = 140
    c: Equal(g0,g1)
FEATURE [PartDesign::Pocket] Pocket002
  BaseFeature = -> Pad001
  Direction = (0,0,-1)
  Length = 5
  Length2 = 5
  Profile = -> Sketch004
  ReferenceAxis = -> Sketch004 [N_Axis]
  Type = 1
FEATURE [PartDesign::Plane] DatumPlane
  AttachmentOffset = pos=(0,0,-10) rot=(0,0,1;0rad)
  Length = 60
  MapMode = 5
  Placement = pos=(0,0,-10) rot=(0,0,1;0rad)
  ResizeMode = 0
  Support = -> [Pocket002]
  Width = 60
FEATURE [Sketcher::SketchObject] Sketch007
  ExternalGeometry = -> [Pocket002]
  FullyConstrained = true
  MapMode = 5
  Support = -> [Pocket002]
  sketch-geometry (4):
    g0: LineSegment StartX=58 StartY=82 StartZ=0 EndX=102 EndY=82 EndZ=0
    g1: LineSegment StartX=102 StartY=82 StartZ=0 EndX=102 EndY=38 EndZ=0
    g2: LineSegment StartX=102 StartY=38 StartZ=0 EndX=58 EndY=38 EndZ=0
    g3: LineSegment StartX=58 StartY=38 StartZ=0 EndX=58 EndY=82 EndZ=0
  constraints (11):
    c: Coincident(g0,g1)
    c: Coincident(g1,g2)
    c: Coincident(g2,g3)
    c: Coincident(g3,g0)
    c: Horizontal(g0)
    c: Horizontal(g2)
    c: Vertical(g1)
    c: Vertical(g3)
    c: DistanceY(g3,g3) = 44
    c: Equal(g3,g0)
    c: Symmetric(g0,g1,g-3)
FEATURE [Sketcher::SketchObject] Sketch008
  ExternalGeometry = -> [Pocket002]
  FullyConstrained = true
  MapMode = 5
  Placement = pos=(0,0,-10) rot=(0,0,1;0rad)
  Support = -> [DatumPlane]
  sketch-geometry (4):
    g0: LineSegment StartX=60.5 StartY=79.5 StartZ=0 EndX=99.5 EndY=79.5 EndZ=0
    g1: LineSegment StartX=99.5 StartY=79.5 StartZ=0 EndX=99.5 EndY=40.5 EndZ=0
    g2: LineSegment StartX=99.5 StartY=40.5 StartZ=0 EndX=60.5 EndY=40.5 EndZ=0
    g3: LineSegment StartX=60.5 StartY=40.5 StartZ=0 EndX=60.5 EndY=79.5 EndZ=0
  constraints (11):
    c: Coincident(g0,g1)
    c: Coincident(g1,g2)
    c: Coincident(g2,g3)
    c: Coincident(g3,g0)
    c: Horizontal(g0)
    c: Horizontal(g2)
    c: Vertical(g1)
    c: Vertical(g3)
    c: DistanceY(g3,g3) = 39
    c: Equal(g3,g0)
    c: Symmetric(g0,g1,g-3)
FEATURE [Sketcher::SketchObject] Sketch009
  ExternalGeometry = -> [Pocket002]
  FullyConstrained = true
  MapMode = 5
  Support = -> [Pocket002]
  sketch-geometry (4):
    g0: LineSegment StartX=78 StartY=162 StartZ=0 EndX=122 EndY=162 EndZ=0
    g1: LineSegment StartX=122 StartY=162 StartZ=0 EndX=122 EndY=118 EndZ=0
    g2: LineSegment StartX=122 StartY=118 StartZ=0 EndX=78 EndY=118 EndZ=0
    g3: LineSegment StartX=78 StartY=118 StartZ=0 EndX=78 EndY=162 EndZ=0
  constraints (11):
    c: Coincident(g0,g1)
    c: Coincident(g1,g2)
    c: Coincident(g2,g3)
    c: Coincident(g3,g0)
    c: Horizontal(g0)
    c: Horizontal(g2)
    c: Vertical(g1)
    c: Vertical(g3)
    c: DistanceY(g3,g3) = 44
    c: Equal(g3,g0)
    c: Symmetric(g0,g1,g-3)
FEATURE [Sketcher::SketchObject] Sketch010
  ExternalGeometry = -> [Pocket002]
  FullyConstrained = true
  MapMode = 5
  Placement = pos=(0,0,-10) rot=(0,0,1;0rad)
  Support = -> [DatumPlane]
  sketch-geometry (4):
    g0: LineSegment StartX=80.5 StartY=159.5 StartZ=0 EndX=119.5 EndY=159.5 EndZ=0
    g1: LineSegment StartX=119.5 StartY=159.5 StartZ=0 EndX=119.5 EndY=120.5 EndZ=0
    g2: LineSegment StartX=119.5 StartY=120.5 StartZ=0 EndX=80.5 EndY=120.5 EndZ=0
    g3: LineSegment StartX=80.5 StartY=120.5 StartZ=0 EndX=80.5 EndY=159.5 EndZ=0
  constraints (11):
    c: Coincident(g0,g1)
    c: Coincident(g1,g2)
    c: Coincident(g2,g3)
    c: Coincident(g3,g0)
    c: Horizontal(g0)
    c: Horizontal(g2)
    c: Vertical(g1)
    c: Vertical(g3)
    c: DistanceY(g3,g3) = 39
    c: Equal(g3,g0)
    c: Symmetric(g0,g1,g-3)
FEATURE [Sketcher::SketchObject] Sketch013  label="Sketch005"
  ExternalGeometry = -> [Pocket002]
  FullyConstrained = true
  MapMode = 5
  Support = -> [Pocket002]
  sketch-geometry (4):
    g0: LineSegment StartX=-22 StartY=102 StartZ=0 EndX=22 EndY=102 EndZ=0
    g1: LineSegment StartX=22 StartY=102 StartZ=0 EndX=22 EndY=58 EndZ=0
    g2: LineSegment StartX=22 StartY=58 StartZ=0 EndX=-22 EndY=58 EndZ=0
    g3: LineSegment StartX=-22 StartY=58 StartZ=0 EndX=-22 EndY=102 EndZ=0
  constraints (11):
    c: Coincident(g0,g1)
    c: Coincident(g1,g2)
    c: Coincident(g2,g3)
    c: Coincident(g3,g0)
    c: Horizontal(g0)
    c: Horizontal(g2)
    c: Vertical(g1)
    c: Vertical(g3)
    c: DistanceY(g3,g3) = 44
    c: Equal(g3,g0)
    c: Symmetric(g0,g1,g-3)
FEATURE [Sketcher::SketchObject] Sketch014  label="Sketch006"
  ExternalGeometry = -> [Pocket002]
  FullyConstrained = true
  MapMode = 5
  Placement = pos=(0,0,-10) rot=(0,0,1;0rad)
  Support = -> [DatumPlane]
  sketch-geometry (4):
    g0: LineSegment StartX=-19.5 StartY=99.5 StartZ=0 EndX=19.5 EndY=99.5 EndZ=0
    g1: LineSegment StartX=19.5 StartY=99.5 StartZ=0 EndX=19.5 EndY=60.5 EndZ=0
    g2: LineSegment StartX=19.5 StartY=60.5 StartZ=0 EndX=-19.5 EndY=60.5 EndZ=0
    g3: LineSegment StartX=-19.5 StartY=60.5 StartZ=0 EndX=-19.5 EndY=99.5 EndZ=0
  constraints (11):
    c: Coincident(g0,g1)
    c: Coincident(g1,g2)
    c: Coincident(g2,g3)
    c: Coincident(g3,g0)
    c: Horizontal(g0)
    c: Horizontal(g2)
    c: Vertical(g1)
    c: Vertical(g3)
    c: DistanceY(g3,g3) = 39
    c: Equal(g0,g3)
    c: Symmetric(g0,g1,g-3)
FEATURE [PartDesign::SubtractiveLoft] SubtractiveLoft
  BaseFeature = -> Pocket002
  Closed = false
  Profile = -> Sketch014
  Ruled = false
  Sections = -> [Sketch013]
FEATURE [PartDesign::SubtractiveLoft] SubtractiveLoft001
  BaseFeature = -> SubtractiveLoft
  Closed = false
  Profile = -> Sketch007
  Ruled = false
  Sections = -> [Sketch008]
FEATURE [PartDesign::SubtractiveLoft] SubtractiveLoft002
  BaseFeature = -> SubtractiveLoft001
  Closed = false
  Profile = -> Sketch009
  Ruled = false
  Sections = -> [Sketch010]
FEATURE [Sketcher::SketchObject] Sketch011
  ExternalGeometry = -> [SubtractiveLoft002]
  FullyConstrained = true
  MapMode = 5
  Support = -> [SubtractiveLoft002]
  sketch-geometry (4):
    g0: LineSegment StartX=118 StartY=22 StartZ=0 EndX=162 EndY=22 EndZ=0
    g1: LineSegment StartX=162 StartY=22 StartZ=0 EndX=162 EndY=-22 EndZ=0
    g2: LineSegment StartX=162 StartY=-22 StartZ=0 EndX=118 EndY=-22 EndZ=0
    g3: LineSegment StartX=118 StartY=-22 StartZ=0 EndX=118 EndY=22 EndZ=0
  constraints (11):
    c: Coincident(g0,g1)
    c: Coincident(g1,g2)
    c: Coincident(g2,g3)
    c: Coincident(g3,g0)
    c: Horizontal(g0)
    c: Horizontal(g2)
    c: Vertical(g1)
    c: Vertical(g3)
    c: DistanceY(g3,g3) = 44
    c: Equal(g3,g0)
    c: Symmetric(g0,g1,g-3)
FEATURE [Sketcher::SketchObject] Sketch012
  ExternalGeometry = -> [SubtractiveLoft002]
  FullyConstrained = true
  MapMode = 5
  Placement = pos=(0,0,-10) rot=(0,0,1;0rad)
  Support = -> [DatumPlane]
  sketch-geometry (4):
    g0: LineSegment StartX=120.5 StartY=19.5 StartZ=0 EndX=159.5 EndY=19.5 EndZ=0
    g1: LineSegment StartX=159.5 StartY=19.5 StartZ=0 EndX=159.5 EndY=-19.5 EndZ=0
    g2: LineSegment StartX=159.5 StartY=-19.5 StartZ=0 EndX=120.5 EndY=-19.5 EndZ=0
    g3: LineSegment StartX=120.5 StartY=-19.5 StartZ=0 EndX=120.5 EndY=19.5 EndZ=0
  constraints (11):
    c: Coincident(g0,g1)
    c: Coincident(g1,g2)
    c: Coincident(g2,g3)
    c: Coincident(g3,g0)
    c: Horizontal(g0)
    c: Horizontal(g2)
    c: Vertical(g1)
    c: Vertical(g3)
    c: DistanceY(g3,g3) = 39
    c: Equal(g3,g0)
    c: Symmetric(g0,g1,g-3)
FEATURE [PartDesign::SubtractiveLoft] SubtractiveLoft003
  BaseFeature = -> SubtractiveLoft002
  Closed = false
  Profile = -> Sketch011
  Ruled = false
  Sections = -> [Sketch012]
FEATURE [PartDesign::Chamfer] Chamfer
  Angle = 45
  Base = -> SubtractiveLoft003 [Edge30,Edge32,Edge33,Edge31,Edge22,Edge24,Edge23,Edge25,Edge37,Edge36,Edge34,Edge35,Edge29,Edge28,Edge26,Edge27]
  BaseFeature = -> SubtractiveLoft003
  ChamferType = 0
  FlipDirection = false
  Size = 1
  Size2 = 1
  SupportTransform = false
  UseAllEdges = false
FEATURE [PartDesign::Fillet] Fillet
  Base = -> Chamfer [Edge9]
  BaseFeature = -> Chamfer
  Radius = 1
  SupportTransform = false
  UseAllEdges = false
FEATURE [PartDesign::Chamfer] Chamfer001
  Angle = 45
  Base = -> Fillet [Edge124,Edge119,Edge132,Edge135,Edge130,Edge113,Edge126,Edge129,Edge116,Edge110,Edge106,Edge101,Edge104,Edge98,Edge109,Edge121,Edge217,Edge299,Edge236,Edge228]
  BaseFeature = -> Fillet
  ChamferType = 0
  FlipDirection = false
  Size = 0.6
  Size2 = 1
  SupportTransform = false
  UseAllEdges = false
FEATURE [PartDesign::Body] Body  label="Main_desk_01-02"
  Group = -> [Sketch,Pad,Sketch001,Pocket,Sketch002,Pocket001,Sketch003,Pad001,Sketch004,Pocket002,DatumPlane,Sketch007,Sketch008,Sketch009,Sketch010,Sketch011,Sketch012,Sketch013,Sketch014,SubtractiveLoft,SubtractiveLoft001,SubtractiveLoft002,SubtractiveLoft003,Chamfer,Fillet,Chamfer001]
  Origin = -> Origin
  Tip = -> Chamfer001
FEATURE [PartDesign::Chamfer] Chamfer003
  Angle = 45
  Base = -> Fillet001 [Edge135,Edge132,Edge129,Edge119,Edge124,Edge121,Edge109,Edge98,Edge104,Edge101,Edge106,Edge110,Edge116,Edge113,Edge126,Edge130]
  BaseFeature = -> Fillet001
  ChamferType = 0
  FlipDirection = false
  Size = 0.6
  Size2 = 1
  SupportTransform = false
  UseAllEdges = false
FEATURE [PartDesign::Body] Body001  label="Main_desk_03-04"
  Group = -> [Sketch015,Pad002,Sketch016,Pocket003,Sketch017,Pocket004,Sketch018,Pad003,Sketch019,Pocket005,DatumPlane001,Sketch020,Sketch021,Sketch022,Sketch023,Sketch024,Sketch025,Sketch026,Sketch027,SubtractiveLoft004,SubtractiveLoft005,SubtractiveLoft006,SubtractiveLoft007,Chamfer002,Fillet001,Chamfer003]
  Origin = -> Origin001
  Tip = -> Chamfer003
FEATURE [TechDraw::DrawSVGTemplate] Template001
  Height = 297
  Orientation = 0
  Template = C:/Program Files/FreeCAD 0.21/data/Mod/TechDraw/Templates/A4_Portrait_blank.svg
  Width = 210
FEATURE [TechDraw::DrawProjGroupItem] ProjItem001  label="Front001"
  CoarseView = false
  Direction = (0,0,1)
  Focus = 100
  HardHidden = false
  IsoCount = 0
  IsoHidden = false
  IsoVisible = false
  LockPosition = true
  Perspective = false
  Rotation = 0
  RotationVector = (1,0,0)
  ScaleType = 2
  ScrubCount = 0
  SeamHidden = false
  SeamVisible = false
  SmoothHidden = false
  SmoothVisible = true
  Source = -> [Body001]
  Type = 0
  X = 0
  XDirection = (1,0,0)
  Y = 0
FEATURE [TechDraw::DrawProjGroup] ProjGroup001
  Anchor = -> ProjItem001
  AutoDistribute = true
  LockPosition = false
  ProjectionType = 0
  Rotation = 0
  Scale = 0.5
  ScaleType = 0
  Source = -> [Body001]
  Views = -> [ProjItem001]
  X = 119.334
  Y = 165.262
  spacingX = 15
  spacingY = 15
FEATURE [TechDraw::DrawViewDimension] Dimension020
  AngleOverride = false
  Arbitrary = false
  ArbitraryTolerances = false
  EqualTolerance = true
  ExtensionAngle = 0
  FormatSpec = %.2w
  FormatSpecOverTolerance = %+.2w
  FormatSpecUnderTolerance = %+.2w
  Inverted = false
  LineAngle = 0
  LockPosition = false
  MeasureType = 1
  OverTolerance = 0
  References2D = -> [ProjItem001]
  Rotation = 0
  Scale = 0.5
  ScaleType = 0
  TheoreticalExact = false
  Type = 1
  UnderTolerance = 0
  X = 44.6125
  Y = 62.2173
FEATURE [TechDraw::DrawViewDimension] Dimension021
  AngleOverride = false
  Arbitrary = false
  ArbitraryTolerances = false
  EqualTolerance = true
  ExtensionAngle = 0
  FormatSpec = %.2w
  FormatSpecOverTolerance = %+.2w
  FormatSpecUnderTolerance = %+.2w
  Inverted = false
  LineAngle = 0
  LockPosition = false
  MeasureType = 1
  OverTolerance = 0
  References2D = -> [ProjItem001]
  Rotation = 0
  Scale = 0.5
  ScaleType = 0
  TheoreticalExact = false
  Type = 2
  UnderTolerance = 0
  X = -97.9212
  Y = 5.65156
FEATURE [TechDraw::DrawViewDimension] Dimension022
  AngleOverride = false
  Arbitrary = false
  ArbitraryTolerances = false
  EqualTolerance = true
  ExtensionAngle = 0
  FormatSpec = %.2w
  FormatSpecOverTolerance = %+.2w
  FormatSpecUnderTolerance = %+.2w
  Inverted = false
  LineAngle = 0
  LockPosition = false
  MeasureType = 1
  OverTolerance = 0
  References2D = -> [ProjItem001]
  Rotation = 0
  Scale = 0.5
  ScaleType = 0
  TheoreticalExact = false
  Type = 2
  UnderTolerance = 0
  X = 68.5047
  Y = 36.9602
FEATURE [TechDraw::DrawViewDimension] Dimension023
  AngleOverride = false
  Arbitrary = false
  ArbitraryTolerances = false
  EqualTolerance = true
  ExtensionAngle = 0
  FormatSpec = %.2w
  FormatSpecOverTolerance = %+.2w
  FormatSpecUnderTolerance = %+.2w
  Inverted = false
  LineAngle = 0
  LockPosition = false
  MeasureType = 1
  OverTolerance = 0
  References2D = -> [ProjItem001]
  Rotation = 0
  Scale = 0.5
  ScaleType = 0
  TheoreticalExact = false
  Type = 1
  UnderTolerance = 0
  X = -0.079282
  Y = -82.8224
FEATURE [TechDraw::DrawViewDimension] Dimension024
  AngleOverride = false
  Arbitrary = false
  ArbitraryTolerances = false
  EqualTolerance = true
  ExtensionAngle = 0
  FormatSpec = %.2w
  FormatSpecOverTolerance = %+.2w
  FormatSpecUnderTolerance = %+.2w
  Inverted = false
  LineAngle = 0
  LockPosition = false
  MeasureType = 1
  OverTolerance = 0
  References2D = -> [ProjItem001]
  Rotation = 0
  Scale = 0.5
  ScaleType = 0
  TheoreticalExact = false
  Type = 1
  UnderTolerance = 0
  X = -40.5734
  Y = -54.0106
FEATURE [TechDraw::DrawViewDimension] Dimension025
  AngleOverride = false
  Arbitrary = false
  ArbitraryTolerances = false
  EqualTolerance = true
  ExtensionAngle = 0
  FormatSpec = %.2w
  FormatSpecOverTolerance = %+.2w
  FormatSpecUnderTolerance = %+.2w
  Inverted = false
  LineAngle = 0
  LockPosition = false
  MeasureType = 1
  OverTolerance = 0
  References2D = -> [ProjItem001]
  Rotation = 0
  Scale = 0.5
  ScaleType = 0
  TheoreticalExact = false
  Type = 1
  UnderTolerance = 0
  X = -30.5734
  Y = -61.0106
FEATURE [TechDraw::DrawViewDimension] Dimension026
  AngleOverride = false
  Arbitrary = false
  ArbitraryTolerances = false
  EqualTolerance = true
  ExtensionAngle = 0
  FormatSpec = %.2w
  FormatSpecOverTolerance = %+.2w
  FormatSpecUnderTolerance = %+.2w
  Inverted = false
  LineAngle = 0
  LockPosition = false
  MeasureType = 1
  OverTolerance = 0
  References2D = -> [ProjItem001]
  Rotation = 0
  Scale = 0.5
  ScaleType = 0
  TheoreticalExact = false
  Type = 1
  UnderTolerance = 0
  X = -15.5734
  Y = -68.0106
FEATURE [TechDraw::DrawViewDimension] Dimension027
  AngleOverride = false
  Arbitrary = false
  ArbitraryTolerances = false
  EqualTolerance = true
  ExtensionAngle = 0
  FormatSpec = %.2w
  FormatSpecOverTolerance = %+.2w
  FormatSpecUnderTolerance = %+.2w
  Inverted = false
  LineAngle = 0
  LockPosition = false
  MeasureType = 1
  OverTolerance = 0
  References2D = -> [ProjItem001]
  Rotation = 0
  Scale = 0.5
  ScaleType = 0
  TheoreticalExact = false
  Type = 1
  UnderTolerance = 0
  X = -0.57339
  Y = -75.0106
FEATURE [TechDraw::DrawViewDimension] Dimension028
  AngleOverride = false
  Arbitrary = false
  ArbitraryTolerances = false
  EqualTolerance = true
  ExtensionAngle = 0
  FormatSpec = %.2w
  FormatSpecOverTolerance = %+.2w
  FormatSpecUnderTolerance = %+.2w
  Inverted = false
  LineAngle = 0
  LockPosition = false
  MeasureType = 1
  OverTolerance = 0
  References2D = -> [ProjItem001]
  Rotation = 0
  Scale = 0.5
  ScaleType = 0
  TheoreticalExact = false
  Type = 2
  UnderTolerance = 0
  X = -69.0672
  Y = -22.2944
FEATURE [TechDraw::DrawViewDimension] Dimension029
  AngleOverride = false
  Arbitrary = false
  ArbitraryTolerances = false
  EqualTolerance = true
  ExtensionAngle = 0
  FormatSpec = %.2w
  FormatSpecOverTolerance = %+.2w
  FormatSpecUnderTolerance = %+.2w
  Inverted = false
  LineAngle = 0
  LockPosition = false
  MeasureType = 1
  OverTolerance = 0
  References2D = -> [ProjItem001]
  Rotation = 0
  Scale = 0.5
  ScaleType = 0
  TheoreticalExact = false
  Type = 2
  UnderTolerance = 0
  X = -76.163
  Y = -8.01109
FEATURE [TechDraw::DrawViewDimension] Dimension030
  AngleOverride = false
  Arbitrary = false
  ArbitraryTolerances = false
  EqualTolerance = true
  ExtensionAngle = 0
  FormatSpec = %.2w
  FormatSpecOverTolerance = %+.2w
  FormatSpecUnderTolerance = %+.2w
  Inverted = false
  LineAngle = 0
  LockPosition = false
  MeasureType = 1
  OverTolerance = 0
  References2D = -> [ProjItem001]
  Rotation = 0
  Scale = 0.5
  ScaleType = 0
  TheoreticalExact = false
  Type = 2
  UnderTolerance = 0
  X = -82.7811
  Y = -3.01109
FEATURE [TechDraw::DrawViewDimension] Dimension031
  AngleOverride = false
  Arbitrary = false
  ArbitraryTolerances = false
  EqualTolerance = true
  ExtensionAngle = 0
  FormatSpec = %.2w
  FormatSpecOverTolerance = %+.2w
  FormatSpecUnderTolerance = %+.2w
  Inverted = false
  LineAngle = 0
  LockPosition = false
  MeasureType = 1
  OverTolerance = 0
  References2D = -> [ProjItem001]
  Rotation = 0
  Scale = 0.5
  ScaleType = 0
  TheoreticalExact = false
  Type = 2
  UnderTolerance = 0
  X = -89.8769
  Y = 2.22783
FEATURE [TechDraw::DrawPage] Page001  label="Front_dwg_03-04"
  KeepUpdated = true
  NextBalloonIndex = 1
  ProjectionType = 0
  Scale = 0.5
  Template = -> Template001
  Views = -> [ProjGroup001,Dimension020,Dimension021,Dimension022,Dimension023,Dimension024,Dimension025,Dimension026,Dimension027,Dimension028,Dimension029,Dimension030,Dimension031]
FEATURE [TechDraw::DrawGeomHatch] GeomHatch001  label="GeomHatch001FX10"
  FilePattern = C:/Program Files/FreeCAD 0.21/data/Mod/TechDraw/PAT/FCPAT.pat
  NamePattern = Diamond
  PatternOffset = (0,0,0)
  PatternRotation = 0
  ScalePattern = 1
  Source = -> ProjItem001 [Face10,Face11]
FEATURE [TechDraw::DrawProjGroupItem] ProjItem  label="Front"
  CoarseView = false
  Direction = (0,0,1)
  Focus = 100
  HardHidden = false
  IsoCount = 0
  IsoHidden = false
  IsoVisible = false
  LockPosition = true
  Perspective = false
  Rotation = 0
  RotationVector = (1,0,0)
  ScaleType = 2
  ScrubCount = 0
  SeamHidden = false
  SeamVisible = false
  SmoothHidden = false
  SmoothVisible = true
  Source = -> [Body]
  Type = 0
  X = 0
  XDirection = (1,0,0)
  Y = 0
FEATURE [TechDraw::DrawProjGroup] ProjGroup
  Anchor = -> ProjItem
  AutoDistribute = true
  LockPosition = false
  ProjectionType = 0
  Rotation = 0
  Scale = 0.5
  ScaleType = 0
  Source = -> [Body]
  Views = -> [ProjItem]
  X = 117.391
  Y = 166.794
  spacingX = 15
  spacingY = 15
FEATURE [TechDraw::DrawViewDimension] Dimension
  AngleOverride = false
  Arbitrary = false
  ArbitraryTolerances = false
  EqualTolerance = true
  ExtensionAngle = 0
  FormatSpec = %.2w
  FormatSpecOverTolerance = %+.2w
  FormatSpecUnderTolerance = %+.2w
  Inverted = false
  LineAngle = 0
  LockPosition = false
  MeasureType = 1
  OverTolerance = 0
  References2D = -> [ProjItem]
  Rotation = 0
  Scale = 0.5
  ScaleType = 0
  TheoreticalExact = false
  Type = 1
  UnderTolerance = 0
  X = 2.15945
  Y = -85.5822
FEATURE [TechDraw::DrawViewDimension] Dimension032
  AngleOverride = false
  Arbitrary = false
  ArbitraryTolerances = false
  EqualTolerance = true
  ExtensionAngle = 0
  FormatSpec = %.2w
  FormatSpecOverTolerance = %+.2w
  FormatSpecUnderTolerance = %+.2w
  Inverted = false
  LineAngle = 0
  LockPosition = false
  MeasureType = 1
  OverTolerance = 0
  References2D = -> [ProjItem]
  Rotation = 0
  Scale = 0.5
  ScaleType = 0
  TheoreticalExact = false
  Type = 2
  UnderTolerance = 0
  X = -95.8837
  Y = 3.6248
FEATURE [TechDraw::DrawViewDimension] Dimension033
  AngleOverride = false
  Arbitrary = false
  ArbitraryTolerances = false
  EqualTolerance = true
  ExtensionAngle = 0
  FormatSpec = %.2w
  FormatSpecOverTolerance = %+.2w
  FormatSpecUnderTolerance = %+.2w
  Inverted = false
  LineAngle = 0
  LockPosition = false
  MeasureType = 1
  OverTolerance = 0
  References2D = -> [ProjItem]
  Rotation = 0
  Scale = 0.5
  ScaleType = 0
  TheoreticalExact = false
  Type = 2
  UnderTolerance = 0
  X = 65.9518
  Y = 36.5156
FEATURE [TechDraw::DrawViewDimension] Dimension034
  AngleOverride = false
  Arbitrary = false
  ArbitraryTolerances = false
  EqualTolerance = true
  ExtensionAngle = 0
  FormatSpec = %.2w
  FormatSpecOverTolerance = %+.2w
  FormatSpecUnderTolerance = %+.2w
  Inverted = false
  LineAngle = 0
  LockPosition = false
  MeasureType = 1
  OverTolerance = 0
  References2D = -> [ProjItem]
  Rotation = 0
  Scale = 0.5
  ScaleType = 0
  TheoreticalExact = false
  Type = 1
  UnderTolerance = 0
  X = 44.297
  Y = 61.9201
FEATURE [TechDraw::DrawViewDimension] Dimension035
  AngleOverride = false
  Arbitrary = false
  ArbitraryTolerances = false
  EqualTolerance = true
  ExtensionAngle = 0
  FormatSpec = %.2w
  FormatSpecOverTolerance = %+.2w
  FormatSpecUnderTolerance = %+.2w
  Inverted = false
  LineAngle = 0
  LockPosition = false
  MeasureType = 1
  OverTolerance = 0
  References2D = -> [ProjItem]
  Rotation = 0
  Scale = 0.5
  ScaleType = 0
  TheoreticalExact = false
  Type = 1
  UnderTolerance = 0
  X = -32.7335
  Y = -54.5714
FEATURE [TechDraw::DrawViewDimension] Dimension036
  AngleOverride = false
  Arbitrary = false
  ArbitraryTolerances = false
  EqualTolerance = true
  ExtensionAngle = 0
  FormatSpec = %.2w
  FormatSpecOverTolerance = %+.2w
  FormatSpecUnderTolerance = %+.2w
  Inverted = false
  LineAngle = 0
  LockPosition = false
  MeasureType = 1
  OverTolerance = 0
  References2D = -> [ProjItem]
  Rotation = 0
  Scale = 0.5
  ScaleType = 0
  TheoreticalExact = false
  Type = 1
  UnderTolerance = 0
  X = -27.9679
  Y = -62.101
FEATURE [TechDraw::DrawViewDimension] Dimension037
  AngleOverride = false
  Arbitrary = false
  ArbitraryTolerances = false
  EqualTolerance = true
  ExtensionAngle = 0
  FormatSpec = %.2w
  FormatSpecOverTolerance = %+.2w
  FormatSpecUnderTolerance = %+.2w
  Inverted = false
  LineAngle = 0
  LockPosition = false
  MeasureType = 1
  OverTolerance = 0
  References2D = -> [ProjItem]
  Rotation = 0
  Scale = 0.5
  ScaleType = 0
  TheoreticalExact = false
  Type = 1
  UnderTolerance = 0
  X = -18.9053
  Y = -69.6307
FEATURE [TechDraw::DrawViewDimension] Dimension038
  AngleOverride = false
  Arbitrary = false
  ArbitraryTolerances = false
  EqualTolerance = true
  ExtensionAngle = 0
  FormatSpec = %.2w
  FormatSpecOverTolerance = %+.2w
  FormatSpecUnderTolerance = %+.2w
  Inverted = false
  LineAngle = 0
  LockPosition = false
  MeasureType = 1
  OverTolerance = 0
  References2D = -> [ProjItem]
  Rotation = 0
  Scale = 0.5
  ScaleType = 0
  TheoreticalExact = false
  Type = 1
  UnderTolerance = 0
  X = -9.84268
  Y = -77.3947
FEATURE [TechDraw::DrawViewDimension] Dimension039
  AngleOverride = false
  Arbitrary = false
  ArbitraryTolerances = false
  EqualTolerance = true
  ExtensionAngle = 0
  FormatSpec = %.2w
  FormatSpecOverTolerance = %+.2w
  FormatSpecUnderTolerance = %+.2w
  Inverted = false
  LineAngle = 0
  LockPosition = false
  MeasureType = 1
  OverTolerance = 0
  References2D = -> [ProjItem]
  Rotation = 0
  Scale = 0.5
  ScaleType = 0
  TheoreticalExact = false
  Type = 2
  UnderTolerance = 0
  X = -71.5986
  Y = -17.7813
FEATURE [TechDraw::DrawViewDimension] Dimension040
  AngleOverride = false
  Arbitrary = false
  ArbitraryTolerances = false
  EqualTolerance = true
  ExtensionAngle = 0
  FormatSpec = %.2w
  FormatSpecOverTolerance = %+.2w
  FormatSpecUnderTolerance = %+.2w
  Inverted = false
  LineAngle = 0
  LockPosition = false
  MeasureType = 1
  OverTolerance = 0
  References2D = -> [ProjItem]
  Rotation = 0
  Scale = 0.5
  ScaleType = 0
  TheoreticalExact = false
  Type = 2
  UnderTolerance = 0
  X = -79.4748
  Y = -12.9932
FEATURE [TechDraw::DrawViewDimension] Dimension041
  AngleOverride = false
  Arbitrary = false
  ArbitraryTolerances = false
  EqualTolerance = true
  ExtensionAngle = 0
  FormatSpec = %.2w
  FormatSpecOverTolerance = %+.2w
  FormatSpecUnderTolerance = %+.2w
  Inverted = false
  LineAngle = 0
  LockPosition = false
  MeasureType = 1
  OverTolerance = 0
  References2D = -> [ProjItem]
  Rotation = 0
  Scale = 0.5
  ScaleType = 0
  TheoreticalExact = false
  Type = 2
  UnderTolerance = 0
  X = -87.8297
  Y = -5.98354
FEATURE [TechDraw::DrawPage] Page  label="Front_dwg_01-02"
  KeepUpdated = true
  NextBalloonIndex = 1
  ProjectionType = 0
  Scale = 0.5
  Template = -> Template
  Views = -> [ProjGroup,Dimension,Dimension032,Dimension033,Dimension034,Dimension035,Dimension036,Dimension037,Dimension038,Dimension039,Dimension040,Dimension041]
FEATURE [TechDraw::DrawGeomHatch] GeomHatch  label="GeomHatchFX11"
  FilePattern = C:/Program Files/FreeCAD 0.21/data/Mod/TechDraw/PAT/FCPAT.pat
  NamePattern = Diamond
  PatternOffset = (0,0,0)
  PatternRotation = 0
  ScalePattern = 1
  Source = -> ProjItem [Face11,Face10]
FEATURE [Sketcher::SketchObject] Sketch028
  FullyConstrained = true
  MapMode = 5
  Support = -> [XY_Plane002]
  sketch-geometry (16):
    g0: LineSegment StartX=-27 StartY=170 StartZ=0 EndX=207 EndY=170 EndZ=0
    g1: LineSegment StartX=210 StartY=167 StartZ=0 EndX=210 EndY=-27 EndZ=0
    g2: LineSegment StartX=207 StartY=-30 StartZ=0 EndX=-27 EndY=-30 EndZ=0
    g3: LineSegment StartX=-30 StartY=-27 StartZ=0 EndX=-30 EndY=167 EndZ=0
    g4: LineSegment StartX=-25 StartY=25 StartZ=0 EndX=25 EndY=25 EndZ=0
    g5: LineSegment StartX=25 StartY=25 StartZ=0 EndX=25 EndY=-25 EndZ=0
    g6: LineSegment StartX=25 StartY=-25 StartZ=0 EndX=-25 EndY=-25 EndZ=0
    g7: LineSegment StartX=-25 StartY=-25 StartZ=0 EndX=-25 EndY=25 EndZ=0
    g8: LineSegment StartX=155 StartY=165 StartZ=0 EndX=205 EndY=165 EndZ=0
    g9: LineSegment StartX=205 StartY=165 StartZ=0 EndX=205 EndY=115 EndZ=0
    g10: LineSegment StartX=205 StartY=115 StartZ=0 EndX=155 EndY=115 EndZ=0
    g11: LineSegment StartX=155 StartY=115 StartZ=0 EndX=155 EndY=165 EndZ=0
    g12: ArcOfCircle CenterX=-27 CenterY=-27 CenterZ=0 NormalX=0 NormalY=0 NormalZ=1 AngleXU=0 Radius=3 StartAngle=3.14159 EndAngle=4.71239
    g13: ArcOfCircle CenterX=207 CenterY=-27 CenterZ=0 NormalX=0 NormalY=0 NormalZ=1 AngleXU=0 Radius=3 StartAngle=4.71239 EndAngle=6.28319
    g14: ArcOfCircle CenterX=207 CenterY=167 CenterZ=0 NormalX=0 NormalY=0 NormalZ=1 AngleXU=0 Radius=3 StartAngle=1.7e-15 EndAngle=1.5708
    g15: ArcOfCircle CenterX=-27 CenterY=167 CenterZ=0 NormalX=0 NormalY=0 NormalZ=1 AngleXU=0 Radius=3 StartAngle=1.5708 EndAngle=3.14159
  constraints (44):
    c: Horizontal(g0)
    c: Horizontal(g2)
    c: Vertical(g1)
    c: Vertical(g3)
    c: Coincident(g4,g5)
    c: Coincident(g5,g6)
    c: Coincident(g6,g7)
    c: Coincident(g7,g4)
    c: Horizontal(g4)
    c: Horizontal(g6)
    c: Vertical(g5)
    c: Vertical(g7)
    c: DistanceY(g7,g7) = 50
    c: Coincident(g8,g9)
    c: Coincident(g9,g10)
    c: Coincident(g10,g11)
    c: Coincident(g11,g8)
    c: Horizontal(g8)
    c: Horizontal(g10)
    c: Vertical(g9)
    c: Vertical(g11)
    c: DistanceY(g9,g9) = 50
    c: DistanceX(g10,g10) = 50
    c: Distance(g9,g1) = 5
    c: Distance(g4,g3) = 5
    c: Distance(g6,g2) = 5
    c: Distance(g8,g0) = 5
    c: DistanceX(g6,g6) = 50
    c: Tangent(g2,g12) = 1.5708
    c: Tangent(g3,g12) = 1.5708
    c: Radius(g12) = 3
    c: Distance(g2,g0) = 200
    c: Tangent(g2,g13) = 1.5708
    c: Tangent(g1,g13) = 1.5708
    c: Tangent(g0,g14) = 1.5708
    c: Tangent(g1,g14) = 1.5708
    c: Tangent(g0,g15) = 1.5708
    c: Tangent(g3,g15) = 1.5708
    c: Equal(g12,g15)
    c: Equal(g12,g14)
    c: Equal(g12,g13)
    c: Distance(g3,g-2) = 30
    c: Distance(g2,g-1) = 30
    c: Distance(g3,g1) = 240
FEATURE [PartDesign::Pad] Pad004
  Direction = (0,0,1)
  Length = 15
  Length2 = 10
  Profile = -> Sketch028
  ReferenceAxis = -> Sketch028 [N_Axis]
  Reversed = true
  Type = 0
FEATURE [Sketcher::SketchObject] Sketch029  label="Sketch_rails_short_003"
  ExternalGeometry = -> [Pad004]
  FullyConstrained = true
  MapMode = 5
  Placement = pos=(210,0,0) rot=(0.57735,0.57735,0.57735;2.0944rad)
  Support = -> [Pad004]
  sketch-geometry (6):
    g0: LineSegment StartX=17.6906 StartY=-15 StartZ=0 EndX=20 EndY=-11 EndZ=0
    g1: LineSegment StartX=20 StartY=-11 StartZ=0 EndX=22.3094 EndY=-15 EndZ=0
    g2: LineSegment StartX=22.3094 StartY=-15 StartZ=0 EndX=17.6906 EndY=-15 EndZ=0
    g3: LineSegment StartX=117.691 StartY=-15 StartZ=0 EndX=120 EndY=-11 EndZ=0
    g4: LineSegment StartX=120 StartY=-11 StartZ=0 EndX=122.309 EndY=-15 EndZ=0
    g5: LineSegment StartX=122.309 StartY=-15 StartZ=0 EndX=117.691 EndY=-15 EndZ=0
  constraints (18):
    c: PointOnObject(g0,g-4)
    c: Coincident(g1,g0)
    c: PointOnObject(g1,g-4)
    c: Coincident(g2,g1)
    c: Coincident(g2,g0)
    c: Distance(g0,g2) = 4
    c: Angle(g0,g-2) = 0.523599
    c: Angle(g-2,g1) = 0.523599
    c: Coincident(g4,g3)
    c: Coincident(g5,g4)
    c: Coincident(g5,g3)
    c: Distance(g3,g5) = 4
    c: Angle(g3,g-2) = 0.523599
    c: Angle(g-2,g4) = 0.523599
    c: PointOnObject(g3,g-4)
    c: PointOnObject(g4,g-4)
    c: Distance(g0,g3) = 100
    c: Distance(g0,g-3) = 50
FEATURE [PartDesign::Pocket] Pocket006
  BaseFeature = -> Pad004
  Direction = (-1,0,0)
  Length = 5
  Length2 = 5
  Profile = -> Sketch029
  ReferenceAxis = -> Sketch029 [N_Axis]
  Type = 1
FEATURE [Sketcher::SketchObject] Sketch030  label="Sketch_rails_long_003"
  ExternalGeometry = -> [Pocket006]
  FullyConstrained = true
  MapMode = 5
  Placement = pos=(0,-30,0) rot=(1,0,0;1.5708rad)
  Support = -> [Pocket006]
  sketch-geometry (7):
    g0: LineSegment StartX=12.6906 StartY=-15 StartZ=0 EndX=15 EndY=-11 EndZ=0
    g1: LineSegment StartX=15 StartY=-11 StartZ=0 EndX=17.3094 EndY=-15 EndZ=0
    g2: LineSegment StartX=17.3094 StartY=-15 StartZ=0 EndX=12.6906 EndY=-15 EndZ=0
    g3: LineSegment StartX=162.691 StartY=-15 StartZ=0 EndX=165 EndY=-11 EndZ=0
    g4: LineSegment StartX=165 StartY=-11 StartZ=0 EndX=167.309 EndY=-15 EndZ=0
    g5: LineSegment StartX=167.309 StartY=-15 StartZ=0 EndX=162.691 EndY=-15 EndZ=0
    g6: LineSegment StartX=-30 StartY=-11 StartZ=0 EndX=210 EndY=-11 EndZ=0
  constraints (22):
    c: PointOnObject(g0,g-4)
    c: Coincident(g1,g0)
    c: PointOnObject(g1,g-4)
    c: Coincident(g2,g0)
    c: PointOnObject(g3,g-4)
    c: PointOnObject(g4,g-4)
    c: Coincident(g5,g3)
    c: Horizontal(g6)
    c: Distance(g-4,g6) = 4
    c: PointOnObject(g0,g6)
    c: PointOnObject(g3,g6)
    c: Coincident(g4,g3)
    c: DistanceX(g6,g6) = 240
    c: PointOnObject(g6,g-3)
    c: Angle(g0,g-2) = 0.523599
    c: Angle(g-2,g1) = 0.523599
    c: Angle(g3,g-2) = 0.523599
    c: Angle(g-2,g4) = 0.523599
    c: Coincident(g2,g1)
    c: Coincident(g5,g4)
    c: Distance(g0,g3) = 150
    c: Distance(g0,g-3) = 45
FEATURE [PartDesign::Pocket] Pocket007
  BaseFeature = -> Pocket006
  Direction = (0,1,-2e-16)
  Length = 5
  Length2 = 5
  Profile = -> Sketch030
  ReferenceAxis = -> Sketch030 [N_Axis]
  Type = 1
FEATURE [Sketcher::SketchObject] Sketch031
  ExternalGeometry = -> [Pocket007]
  FullyConstrained = false
  MapMode = 5
  Support = -> [Pocket007]
  sketch-geometry (40):
    g0: LineSegment StartX=-18 StartY=18 StartZ=0 EndX=18 EndY=18 EndZ=0
    g1: LineSegment StartX=18 StartY=18 StartZ=0 EndX=18 EndY=-18 EndZ=0
    g2: LineSegment StartX=-18 StartY=-18 StartZ=0 EndX=-18 EndY=18 EndZ=0
    g3: LineSegment StartX=180 StartY=170 StartZ=0 EndX=180 EndY=-30 EndZ=0
    g4: LineSegment StartX=-30 StartY=140 StartZ=0 EndX=210 EndY=140 EndZ=0
    g5: LineSegment StartX=162 StartY=158 StartZ=0 EndX=198 EndY=158 EndZ=0
    g6: LineSegment StartX=198 StartY=158 StartZ=0 EndX=198 EndY=122 EndZ=0
    g7: LineSegment StartX=198 StartY=122 StartZ=0 EndX=162 EndY=122 EndZ=0
    g8: LineSegment StartX=162 StartY=122 StartZ=0 EndX=162 EndY=158 EndZ=0
    g9: LineSegment StartX=-12 StartY=-12 StartZ=0 EndX=-12 EndY=6 EndZ=0
    g10: LineSegment StartX=-6 StartY=6 StartZ=0 EndX=-12 EndY=6 EndZ=0
    g11: LineSegment StartX=-6 StartY=6 StartZ=0 EndX=-6 EndY=12 EndZ=0
    g12: LineSegment StartX=-6 StartY=12 StartZ=0 EndX=12 EndY=12 EndZ=0
    g13: LineSegment StartX=12 StartY=12 StartZ=0 EndX=12 EndY=0 EndZ=0
    g14: LineSegment StartX=12 StartY=0 StartZ=0 EndX=6 EndY=0 EndZ=0
    g15: LineSegment StartX=6 StartY=0 StartZ=0 EndX=6 EndY=6 EndZ=0
    g16: LineSegment StartX=6 StartY=6 StartZ=0 EndX=-6 EndY=6 EndZ=0
    g17: LineSegment StartX=-6 StartY=6 StartZ=0 EndX=-6 EndY=0 EndZ=0
    g18: LineSegment StartX=-6 StartY=0 StartZ=0 EndX=0 EndY=0 EndZ=0
    g19: LineSegment StartX=0 StartY=0 StartZ=0 EndX=0 EndY=-12 EndZ=0
    g20: LineSegment StartX=0 StartY=-12 StartZ=0 EndX=-12 EndY=-12 EndZ=0
    g21: LineSegment StartX=6 StartY=-12 StartZ=0 EndX=6 EndY=-6 EndZ=0
    g22: LineSegment StartX=6 StartY=-6 StartZ=0 EndX=12 EndY=-6 EndZ=0
    g23: LineSegment StartX=12 StartY=-6 StartZ=0 EndX=12 EndY=-12 EndZ=0
    g24: LineSegment StartX=12 StartY=-12 StartZ=0 EndX=6 EndY=-12 EndZ=0
    g25: LineSegment StartX=-18 StartY=-18 StartZ=0 EndX=18 EndY=-18 EndZ=0
    g26: LineSegment StartX=168 StartY=128 StartZ=0 EndX=168 EndY=134 EndZ=0
    g27: LineSegment StartX=168 StartY=134 StartZ=0 EndX=180 EndY=134 EndZ=0
    g28: LineSegment StartX=180 StartY=134 StartZ=0 EndX=180 EndY=140 EndZ=0
    g29: LineSegment StartX=180 StartY=140 StartZ=0 EndX=168 EndY=140 EndZ=0
    g30: LineSegment StartX=168 StartY=140 StartZ=0 EndX=168 EndY=152 EndZ=0
    g31: LineSegment StartX=168 StartY=152 StartZ=0 EndX=174 EndY=152 EndZ=0
    g32: LineSegment StartX=174 StartY=152 StartZ=0 EndX=174 EndY=146 EndZ=0
    g33: LineSegment StartX=174 StartY=146 StartZ=0 EndX=186 EndY=146 EndZ=0
    g34: LineSegment StartX=186 StartY=146 StartZ=0 EndX=186 EndY=152 EndZ=0
    g35: LineSegment StartX=186 StartY=152 StartZ=0 EndX=192 EndY=152 EndZ=0
    g36: LineSegment StartX=192 StartY=152 StartZ=0 EndX=192 EndY=146 EndZ=0
    g37: LineSegment StartX=192 StartY=146 StartZ=0 EndX=186 EndY=146 EndZ=0
    g38: LineSegment StartX=186 StartY=146 StartZ=0 EndX=186 EndY=128 EndZ=0
    g39: LineSegment StartX=186 StartY=128 StartZ=0 EndX=168 EndY=128 EndZ=0
  constraints (109):
    c: Coincident(g0,g1)
    c: Coincident(g2,g0)
    c: Horizontal(g0)
    c: Vertical(g1)
    c: DistanceX(g2,g1) = 36
    c: Symmetric(g2,g1,g-2)
    c: Symmetric(g0,g2,g-1)
    c: Vertical(g3)
    c: Horizontal(g4)
    c: PointOnObject(g3,g-4)
    c: PointOnObject(g4,g-5)
    c: PointOnObject(g4,g-3)
    c: Distance(g4,g-1) = 140
    c: Distance(g3,g-2) = 180
    c: Coincident(g5,g6)
    c: Coincident(g6,g7)
    c: Coincident(g7,g8)
    c: Coincident(g8,g5)
    c: Horizontal(g5)
    c: Horizontal(g7)
    c: Vertical(g6)
    c: Vertical(g8)
    c: DistanceY(g6,g6) = 36
    c: Equal(g5,g6)
    c: Distance(g5,g4) = 18
    c: Distance(g5,g3) = 18
    c: Vertical(g9)
    c: Coincident(g10,g9)
    c: Coincident(g10,g11)
    c: Vertical(g11)
    c: Coincident(g11,g12)
    c: Horizontal(g12)
    c: Coincident(g12,g13)
    c: Vertical(g13)
    c: Coincident(g13,g14)
    c: Horizontal(g14)
    c: Coincident(g14,g15)
    c: Vertical(g15)
    c: Coincident(g15,g16)
    c: Horizontal(g16)
    c: Coincident(g16,g17)
    c: Coincident(g17,g18)
    c: Coincident(g18,g19)
    c: Vertical(g19)
    c: Coincident(g19,g20)
    c: Coincident(g20,g9)
    c: Horizontal(g20)
    c: Coincident(g21,g22)
    c: Horizontal(g22)
    c: Coincident(g22,g23)
    c: Coincident(g23,g24)
    c: Coincident(g24,g21)
    c: Distance(g9,g2) = 6
    c: DistanceX(g10,g10) = 6
    c: DistanceX(g18,g18) = 6
    c: Tangent(g11,g17)
    c: Tangent(g10,g16)
    c: Tangent(g20,g24)
    c: Tangent(g15,g21)
    c: Tangent(g13,g23)
    c: Tangent(g18,g14)
    c: Distance(g21,g19) = 6
    c: Distance(g24) = 6
    c: DistanceY(g23,g23) = 6
    c: DistanceY(g15,g15) = 6
    c: DistanceY(g11,g11) = 6
    c: Distance(g14,g22) = 6
    c: Coincident(g25,g2)
    c: Coincident(g25,g1)
    c: Equal(g2,g8)
    c: Distance(g9,g25) = 6
    c: Vertical(g26)
    c: Coincident(g26,g27)
    c: Horizontal(g27)
    c: Coincident(g27,g28)
    c: Vertical(g28)
    c: Coincident(g28,g29)
    c: Horizontal(g29)
    c: Coincident(g29,g30)
    c: Coincident(g30,g31)
    c: Horizontal(g31)
    c: Coincident(g31,g32)
    c: Vertical(g32)
    c: Coincident(g32,g33)
    c: Horizontal(g33)
    c: Coincident(g33,g34)
    c: Vertical(g34)
    c: Coincident(g34,g35)
    c: Coincident(g35,g36)
    c: Vertical(g36)
    c: Coincident(g36,g37)
    c: Coincident(g37,g38)
    c: Coincident(g38,g39)
    c: Coincident(g39,g26)
    c: Horizontal(g39)
    c: Tangent(g30,g26)
    c: Tangent(g34,g38)
    c: Tangent(g31,g35)
    c: Tangent(g33,g37)
    c: DistanceX(g31,g31) = 6
    c: Distance(g30,g8) = 6
    c: Distance(g28,g32) = 6
    c: Distance(g28,g38) = 6
    c: DistanceX(g35,g35) = 6
    c: Distance(g35,g5) = 6
    c: DistanceY(g36,g36) = 6
    c: DistanceY(g28,g28) = 6
    c: Distance(g28,g33) = 6
    c: Distance(g27,g39) = 6
FEATURE [PartDesign::Pad] Pad005
  BaseFeature = -> Pocket007
  Direction = (0,0,1)
  Length = 0.6
  Length2 = 10
  Profile = -> Sketch031
  ReferenceAxis = -> Sketch031 [N_Axis]
  Type = 0
FEATURE [Sketcher::SketchObject] Sketch032
  FullyConstrained = true
  MapMode = 5
  Support = -> [Pad005]
  sketch-geometry (4):
    g0: Circle CenterX=0 CenterY=140 CenterZ=0 NormalX=0 NormalY=0 NormalZ=1 AngleXU=0 Radius=8
    g1: Circle CenterX=80 CenterY=80 CenterZ=0 NormalX=0 NormalY=0 NormalZ=1 AngleXU=0 Radius=8
    g2: Circle CenterX=160 CenterY=60 CenterZ=0 NormalX=0 NormalY=0 NormalZ=1 AngleXU=0 Radius=8
    g3: Circle CenterX=60 CenterY=0 CenterZ=0 NormalX=0 NormalY=0 NormalZ=1 AngleXU=0 Radius=8
  constraints (12):
    c: Diameter(g0) = 16
    c: Distance(g2,g-2) = 160
    c: Equal(g2,g0)
    c: Distance(g3,g-2) = 60
    c: Equal(g3,g0)
    c: Distance(g1,g-2) = 80
    c: Distance(g1,g-1) = 80
    c: Equal(g0,g1)
    c: Distance(g0,g-1) = 140
    c: PointOnObject(g0,g-2)
    c: PointOnObject(g3,g-1)
    c: Distance(g2,g-1) = 60
FEATURE [PartDesign::Pocket] Pocket008
  BaseFeature = -> Pad005
  Direction = (0,0,-1)
  Length = 5
  Length2 = 5
  Profile = -> Sketch032
  ReferenceAxis = -> Sketch032 [N_Axis]
  Type = 1
FEATURE [PartDesign::Plane] DatumPlane002
  AttachmentOffset = pos=(0,0,-10) rot=(0,0,1;0rad)
  Length = 60
  MapMode = 5
  Placement = pos=(0,0,-10) rot=(0,0,1;0rad)
  ResizeMode = 0
  Support = -> [Pocket008]
  Width = 60
FEATURE [Sketcher::SketchObject] Sketch033
  ExternalGeometry = -> [Pocket008]
  FullyConstrained = true
  MapMode = 5
  Support = -> [Pocket008]
  sketch-geometry (4):
    g0: LineSegment StartX=38 StartY=22 StartZ=0 EndX=82 EndY=22 EndZ=0
    g1: LineSegment StartX=82 StartY=22 StartZ=0 EndX=82 EndY=-22 EndZ=0
    g2: LineSegment StartX=82 StartY=-22 StartZ=0 EndX=38 EndY=-22 EndZ=0
    g3: LineSegment StartX=38 StartY=-22 StartZ=0 EndX=38 EndY=22 EndZ=0
  constraints (11):
    c: Coincident(g0,g1)
    c: Coincident(g1,g2)
    c: Coincident(g2,g3)
    c: Coincident(g3,g0)
    c: Horizontal(g0)
    c: Horizontal(g2)
    c: Vertical(g1)
    c: Vertical(g3)
    c: DistanceY(g3,g3) = 44
    c: Equal(g3,g0)
    c: Symmetric(g0,g1,g-3)
FEATURE [Sketcher::SketchObject] Sketch034
  ExternalGeometry = -> [Pocket008]
  FullyConstrained = true
  MapMode = 5
  Placement = pos=(0,0,-10) rot=(0,0,1;0rad)
  Support = -> [DatumPlane002]
  sketch-geometry (4):
    g0: LineSegment StartX=40.5 StartY=19.5 StartZ=0 EndX=79.5 EndY=19.5 EndZ=0
    g1: LineSegment StartX=79.5 StartY=19.5 StartZ=0 EndX=79.5 EndY=-19.5 EndZ=0
    g2: LineSegment StartX=79.5 StartY=-19.5 StartZ=0 EndX=40.5 EndY=-19.5 EndZ=0
    g3: LineSegment StartX=40.5 StartY=-19.5 StartZ=0 EndX=40.5 EndY=19.5 EndZ=0
  constraints (11):
    c: Coincident(g0,g1)
    c: Coincident(g1,g2)
    c: Coincident(g2,g3)
    c: Coincident(g3,g0)
    c: Horizontal(g0)
    c: Horizontal(g2)
    c: Vertical(g1)
    c: Vertical(g3)
    c: DistanceY(g3,g3) = 39
    c: Equal(g3,g0)
    c: Symmetric(g0,g1,g-3)
FEATURE [Sketcher::SketchObject] Sketch035
  ExternalGeometry = -> [Pocket008]
  FullyConstrained = true
  MapMode = 5
  Support = -> [Pocket008]
  sketch-geometry (4):
    g0: LineSegment StartX=22 StartY=162 StartZ=0 EndX=-22 EndY=162 EndZ=0
    g1: LineSegment StartX=-22 StartY=162 StartZ=0 EndX=-22 EndY=118 EndZ=0
    g2: LineSegment StartX=-22 StartY=118 StartZ=0 EndX=22 EndY=118 EndZ=0
    g3: LineSegment StartX=22 StartY=118 StartZ=0 EndX=22 EndY=162 EndZ=0
  constraints (11):
    c: Coincident(g0,g1)
    c: Coincident(g1,g2)
    c: Coincident(g2,g3)
    c: Coincident(g3,g0)
    c: Horizontal(g0)
    c: Horizontal(g2)
    c: Vertical(g1)
    c: Vertical(g3)
    c: DistanceY(g3,g3) = 44
    c: Equal(g3,g0)
    c: Symmetric(g0,g1,g-3)
FEATURE [Sketcher::SketchObject] Sketch036
  ExternalGeometry = -> [Pocket008]
  FullyConstrained = true
  MapMode = 5
  Placement = pos=(0,0,-10) rot=(0,0,1;0rad)
  Support = -> [DatumPlane002]
  sketch-geometry (4):
    g0: LineSegment StartX=19.5 StartY=159.5 StartZ=0 EndX=-19.5 EndY=159.5 EndZ=0
    g1: LineSegment StartX=-19.5 StartY=159.5 StartZ=0 EndX=-19.5 EndY=120.5 EndZ=0
    g2: LineSegment StartX=-19.5 StartY=120.5 StartZ=0 EndX=19.5 EndY=120.5 EndZ=0
    g3: LineSegment StartX=19.5 StartY=120.5 StartZ=0 EndX=19.5 EndY=159.5 EndZ=0
  constraints (11):
    c: Coincident(g0,g1)
    c: Coincident(g1,g2)
    c: Coincident(g2,g3)
    c: Coincident(g3,g0)
    c: Horizontal(g0)
    c: Horizontal(g2)
    c: Vertical(g1)
    c: Vertical(g3)
    c: DistanceY(g3,g3) = 39
    c: Equal(g3,g0)
    c: Symmetric(g0,g1,g-3)
FEATURE [Sketcher::SketchObject] Sketch039
  ExternalGeometry = -> [Pocket008]
  FullyConstrained = true
  MapMode = 5
  Support = -> [Pocket008]
  sketch-geometry (4):
    g0: LineSegment StartX=58 StartY=102 StartZ=0 EndX=102 EndY=102 EndZ=0
    g1: LineSegment StartX=102 StartY=102 StartZ=0 EndX=102 EndY=58 EndZ=0
    g2: LineSegment StartX=102 StartY=58 StartZ=0 EndX=58 EndY=58 EndZ=0
    g3: LineSegment StartX=58 StartY=58 StartZ=0 EndX=58 EndY=102 EndZ=0
  constraints (11):
    c: Coincident(g0,g1)
    c: Coincident(g1,g2)
    c: Coincident(g2,g3)
    c: Coincident(g3,g0)
    c: Horizontal(g0)
    c: Horizontal(g2)
    c: Vertical(g1)
    c: Vertical(g3)
    c: DistanceY(g3,g3) = 44
    c: Equal(g3,g0)
    c: Symmetric(g0,g1,g-3)
FEATURE [Sketcher::SketchObject] Sketch040
  ExternalGeometry = -> [Pocket008]
  FullyConstrained = true
  MapMode = 5
  Placement = pos=(0,0,-10) rot=(0,0,1;0rad)
  Support = -> [DatumPlane002]
  sketch-geometry (4):
    g0: LineSegment StartX=60.5 StartY=99.5 StartZ=0 EndX=99.5 EndY=99.5 EndZ=0
    g1: LineSegment StartX=99.5 StartY=99.5 StartZ=0 EndX=99.5 EndY=60.5 EndZ=0
    g2: LineSegment StartX=99.5 StartY=60.5 StartZ=0 EndX=60.5 EndY=60.5 EndZ=0
    g3: LineSegment StartX=60.5 StartY=60.5 StartZ=0 EndX=60.5 EndY=99.5 EndZ=0
  constraints (11):
    c: Coincident(g0,g1)
    c: Coincident(g1,g2)
    c: Coincident(g2,g3)
    c: Coincident(g3,g0)
    c: Horizontal(g0)
    c: Horizontal(g2)
    c: Vertical(g1)
    c: Vertical(g3)
    c: DistanceY(g3,g3) = 39
    c: Equal(g0,g3)
    c: Symmetric(g0,g1,g-3)
FEATURE [PartDesign::SubtractiveLoft] SubtractiveLoft008
  BaseFeature = -> Pocket008
  Closed = false
  Profile = -> Sketch040
  Ruled = false
  Sections = -> [Sketch039]
FEATURE [PartDesign::SubtractiveLoft] SubtractiveLoft009
  BaseFeature = -> SubtractiveLoft008
  Closed = false
  Profile = -> Sketch033
  Ruled = false
  Sections = -> [Sketch034]
FEATURE [PartDesign::SubtractiveLoft] SubtractiveLoft010
  BaseFeature = -> SubtractiveLoft009
  Closed = false
  Profile = -> Sketch035
  Ruled = false
  Sections = -> [Sketch036]
FEATURE [Sketcher::SketchObject] Sketch037
  ExternalGeometry = -> [SubtractiveLoft010]
  FullyConstrained = true
  MapMode = 5
  Support = -> [SubtractiveLoft010]
  sketch-geometry (4):
    g0: LineSegment StartX=138 StartY=82 StartZ=0 EndX=182 EndY=82 EndZ=0
    g1: LineSegment StartX=182 StartY=82 StartZ=0 EndX=182 EndY=38 EndZ=0
    g2: LineSegment StartX=182 StartY=38 StartZ=0 EndX=138 EndY=38 EndZ=0
    g3: LineSegment StartX=138 StartY=38 StartZ=0 EndX=138 EndY=82 EndZ=0
  constraints (11):
    c: Coincident(g0,g1)
    c: Coincident(g1,g2)
    c: Coincident(g2,g3)
    c: Coincident(g3,g0)
    c: Horizontal(g0)
    c: Horizontal(g2)
    c: Vertical(g1)
    c: Vertical(g3)
    c: DistanceY(g3,g3) = 44
    c: Equal(g3,g0)
    c: Symmetric(g0,g1,g-3)
FEATURE [Sketcher::SketchObject] Sketch038
  ExternalGeometry = -> [SubtractiveLoft010]
  FullyConstrained = true
  MapMode = 5
  Placement = pos=(0,0,-10) rot=(0,0,1;0rad)
  Support = -> [DatumPlane002]
  sketch-geometry (4):
    g0: LineSegment StartX=140.5 StartY=79.5 StartZ=0 EndX=179.5 EndY=79.5 EndZ=0
    g1: LineSegment StartX=179.5 StartY=79.5 StartZ=0 EndX=179.5 EndY=40.5 EndZ=0
    g2: LineSegment StartX=179.5 StartY=40.5 StartZ=0 EndX=140.5 EndY=40.5 EndZ=0
    g3: LineSegment StartX=140.5 StartY=40.5 StartZ=0 EndX=140.5 EndY=79.5 EndZ=0
  constraints (11):
    c: Coincident(g0,g1)
    c: Coincident(g1,g2)
    c: Coincident(g2,g3)
    c: Coincident(g3,g0)
    c: Horizontal(g0)
    c: Horizontal(g2)
    c: Vertical(g1)
    c: Vertical(g3)
    c: DistanceY(g3,g3) = 39
    c: Equal(g3,g0)
    c: Symmetric(g0,g1,g-3)
FEATURE [PartDesign::SubtractiveLoft] SubtractiveLoft011
  BaseFeature = -> SubtractiveLoft010
  Closed = false
  Profile = -> Sketch037
  Ruled = false
  Sections = -> [Sketch038]
FEATURE [PartDesign::Chamfer] Chamfer004
  Angle = 45
  Base = -> SubtractiveLoft011 [Edge30,Edge32,Edge33,Edge31,Edge22,Edge24,Edge23,Edge25,Edge37,Edge36,Edge34,Edge35,Edge29,Edge28,Edge26,Edge27]
  BaseFeature = -> SubtractiveLoft011
  ChamferType = 0
  FlipDirection = false
  Size = 1
  Size2 = 1
  SupportTransform = false
  UseAllEdges = false
FEATURE [PartDesign::Fillet] Fillet002
  Base = -> Chamfer004 [Edge9]
  BaseFeature = -> Chamfer004
  Radius = 1
  SupportTransform = false
  UseAllEdges = false
FEATURE [PartDesign::Chamfer] Chamfer005
  Angle = 45
  Base = -> Fillet002 [Edge135,Edge132,Edge129,Edge119,Edge124,Edge121,Edge109,Edge98,Edge104,Edge101,Edge106,Edge110,Edge116,Edge113,Edge126,Edge130]
  BaseFeature = -> Fillet002
  ChamferType = 0
  FlipDirection = false
  Size = 0.6
  Size2 = 1
  SupportTransform = false
  UseAllEdges = false
FEATURE [PartDesign::Chamfer] Chamfer006
  Angle = 45
  Base = -> Chamfer005 [Edge218,Edge294,Edge198,Edge288,Edge365,Edge306,Edge195,Edge304]
  BaseFeature = -> Chamfer005
  ChamferType = 0
  FlipDirection = false
  Size = 0.6
  Size2 = 1
  SupportTransform = false
  UseAllEdges = false
FEATURE [PartDesign::Body] Body002  label="Main_desk_05-06"
  Group = -> [Sketch028,Pad004,Sketch029,Pocket006,Sketch030,Pocket007,Sketch031,Pad005,Sketch032,Pocket008,DatumPlane002,Sketch033,Sketch034,Sketch035,Sketch036,Sketch037,Sketch038,Sketch039,Sketch040,SubtractiveLoft008,SubtractiveLoft009,SubtractiveLoft010,SubtractiveLoft011,Chamfer004,Fillet002,Chamfer005,Chamfer006]
  Origin = -> Origin002
  Tip = -> Chamfer006
FEATURE [TechDraw::DrawSVGTemplate] Template002
  Height = 297
  Orientation = 0
  Template = C:/Program Files/FreeCAD 0.21/data/Mod/TechDraw/Templates/A4_Portrait_blank.svg
  Width = 210
FEATURE [TechDraw::DrawProjGroupItem] ProjItem002  label="Front002"
  CoarseView = false
  Direction = (0,0,1)
  Focus = 100
  HardHidden = false
  IsoCount = 0
  IsoHidden = false
  IsoVisible = false
  LockPosition = true
  Perspective = false
  Rotation = 0
  RotationVector = (1,0,0)
  ScaleType = 2
  ScrubCount = 0
  SeamHidden = false
  SeamVisible = false
  SmoothHidden = false
  SmoothVisible = true
  Source = -> [Chamfer006]
  Type = 0
  X = 0
  XDirection = (1,0,0)
  Y = 0
FEATURE [TechDraw::DrawProjGroup] ProjGroup002
  Anchor = -> ProjItem002
  AutoDistribute = true
  LockPosition = false
  ProjectionType = 0
  Rotation = 0
  Scale = 0.5
  ScaleType = 0
  Source = -> [Chamfer006]
  Views = -> [ProjItem002]
  X = 118.612
  Y = 163.305
  spacingX = 15
  spacingY = 15
FEATURE [TechDraw::DrawGeomHatch] GeomHatch002  label="GeomHatch002FX11"
  FilePattern = C:/Program Files/FreeCAD 0.21/data/Mod/TechDraw/PAT/FCPAT.pat
  NamePattern = Diamond
  PatternOffset = (0,0,0)
  PatternRotation = 0
  ScalePattern = 1
  Source = -> ProjItem002 [Face11]
FEATURE [TechDraw::DrawGeomHatch] GeomHatch003  label="GeomHatch003FX10"
  FilePattern = C:/Program Files/FreeCAD 0.21/data/Mod/TechDraw/PAT/FCPAT.pat
  NamePattern = Diamond
  PatternOffset = (0,0,0)
  PatternRotation = 0
  ScalePattern = 1
  Source = -> ProjItem002 [Face10]
FEATURE [TechDraw::DrawViewDimension] Dimension042
  AngleOverride = false
  Arbitrary = false
  ArbitraryTolerances = false
  EqualTolerance = true
  ExtensionAngle = 0
  FormatSpec = %.2w
  FormatSpecOverTolerance = %+.2w
  FormatSpecUnderTolerance = %+.2w
  Inverted = false
  LineAngle = 0
  LockPosition = false
  MeasureType = 1
  OverTolerance = 0
  References2D = -> [ProjItem002]
  Rotation = 0
  Scale = 0.5
  ScaleType = 0
  TheoreticalExact = false
  Type = 1
  UnderTolerance = 0
  X = -30
  Y = -54.1074
FEATURE [TechDraw::DrawViewDimension] Dimension043
  AngleOverride = false
  Arbitrary = false
  ArbitraryTolerances = false
  EqualTolerance = true
  ExtensionAngle = 0
  FormatSpec = %.2w
  FormatSpecOverTolerance = %+.2w
  FormatSpecUnderTolerance = %+.2w
  Inverted = false
  LineAngle = 0
  LockPosition = false
  MeasureType = 1
  OverTolerance = 0
  References2D = -> [ProjItem002]
  Rotation = 0
  Scale = 0.5
  ScaleType = 0
  TheoreticalExact = false
  Type = 1
  UnderTolerance = 0
  X = -26.1872
  Y = -62.5405
FEATURE [TechDraw::DrawViewDimension] Dimension044
  AngleOverride = false
  Arbitrary = false
  ArbitraryTolerances = false
  EqualTolerance = true
  ExtensionAngle = 0
  FormatSpec = %.2w
  FormatSpecOverTolerance = %+.2w
  FormatSpecUnderTolerance = %+.2w
  Inverted = false
  LineAngle = 0
  LockPosition = false
  MeasureType = 1
  OverTolerance = 0
  References2D = -> [ProjItem002]
  Rotation = 0
  Scale = 0.5
  ScaleType = 0
  TheoreticalExact = false
  Type = 1
  UnderTolerance = 0
  X = -22.8075
  Y = -71.7651
FEATURE [TechDraw::DrawViewDimension] Dimension045
  AngleOverride = false
  Arbitrary = false
  ArbitraryTolerances = false
  EqualTolerance = true
  ExtensionAngle = 0
  FormatSpec = %.2w
  FormatSpecOverTolerance = %+.2w
  FormatSpecUnderTolerance = %+.2w
  Inverted = false
  LineAngle = 0
  LockPosition = false
  MeasureType = 1
  OverTolerance = 0
  References2D = -> [ProjItem002]
  Rotation = 0
  Scale = 0.5
  ScaleType = 0
  TheoreticalExact = false
  Type = 1
  UnderTolerance = 0
  X = -18.2032
  Y = -80.9896
FEATURE [TechDraw::DrawViewDimension] Dimension046
  AngleOverride = false
  Arbitrary = false
  ArbitraryTolerances = false
  EqualTolerance = true
  ExtensionAngle = 0
  FormatSpec = %.2w
  FormatSpecOverTolerance = %+.2w
  FormatSpecUnderTolerance = %+.2w
  Inverted = false
  LineAngle = 0
  LockPosition = false
  MeasureType = 1
  OverTolerance = 0
  References2D = -> [ProjItem002]
  Rotation = 0
  Scale = 0.5
  ScaleType = 0
  TheoreticalExact = false
  Type = 2
  UnderTolerance = 0
  X = -68.2095
  Y = -21.3561
FEATURE [TechDraw::DrawViewDimension] Dimension047
  AngleOverride = false
  Arbitrary = false
  ArbitraryTolerances = false
  EqualTolerance = true
  ExtensionAngle = 0
  FormatSpec = %.2w
  FormatSpecOverTolerance = %+.2w
  FormatSpecUnderTolerance = %+.2w
  Inverted = false
  LineAngle = 0
  LockPosition = false
  MeasureType = 1
  OverTolerance = 0
  References2D = -> [ProjItem002]
  Rotation = 0
  Scale = 0.5
  ScaleType = 0
  TheoreticalExact = false
  Type = 2
  UnderTolerance = 0
  X = -76.1414
  Y = -16.3561
FEATURE [TechDraw::DrawViewDimension] Dimension048
  AngleOverride = false
  Arbitrary = false
  ArbitraryTolerances = false
  EqualTolerance = true
  ExtensionAngle = 0
  FormatSpec = %.2w
  FormatSpecOverTolerance = %+.2w
  FormatSpecUnderTolerance = %+.2w
  Inverted = false
  LineAngle = 0
  LockPosition = false
  MeasureType = 1
  OverTolerance = 0
  References2D = -> [ProjItem002]
  Rotation = 0
  Scale = 0.5
  ScaleType = 0
  TheoreticalExact = false
  Type = 2
  UnderTolerance = 0
  X = -83.452
  Y = -10.9849
FEATURE [TechDraw::DrawViewDimension] Dimension049
  AngleOverride = false
  Arbitrary = false
  ArbitraryTolerances = false
  EqualTolerance = true
  ExtensionAngle = 0
  FormatSpec = %.2w
  FormatSpecOverTolerance = %+.2w
  FormatSpecUnderTolerance = %+.2w
  Inverted = false
  LineAngle = 0
  LockPosition = false
  MeasureType = 1
  OverTolerance = 0
  References2D = -> [ProjItem002]
  Rotation = 0
  Scale = 0.5
  ScaleType = 0
  TheoreticalExact = false
  Type = 1
  UnderTolerance = 0
  X = -3.39728
  Y = -89.4587
FEATURE [TechDraw::DrawViewDimension] Dimension050
  AngleOverride = false
  Arbitrary = false
  ArbitraryTolerances = false
  EqualTolerance = true
  ExtensionAngle = 0
  FormatSpec = %.2w
  FormatSpecOverTolerance = %+.2w
  FormatSpecUnderTolerance = %+.2w
  Inverted = false
  LineAngle = 0
  LockPosition = false
  MeasureType = 1
  OverTolerance = 0
  References2D = -> [ProjItem002]
  Rotation = 0
  Scale = 0.5
  ScaleType = 0
  TheoreticalExact = false
  Type = 2
  UnderTolerance = 0
  X = -91.9223
  Y = 2.59258
FEATURE [TechDraw::DrawViewDimension] Dimension051
  AngleOverride = false
  Arbitrary = false
  ArbitraryTolerances = false
  EqualTolerance = true
  ExtensionAngle = 0
  FormatSpec = %.2w
  FormatSpecOverTolerance = %+.2w
  FormatSpecUnderTolerance = %+.2w
  Inverted = false
  LineAngle = 0
  LockPosition = false
  MeasureType = 1
  OverTolerance = 0
  References2D = -> [ProjItem002]
  Rotation = 0
  Scale = 0.5
  ScaleType = 0
  TheoreticalExact = false
  Type = 1
  UnderTolerance = 0
  X = 45
  Y = 58.9559
FEATURE [TechDraw::DrawViewDimension] Dimension052
  AngleOverride = false
  Arbitrary = false
  ArbitraryTolerances = false
  EqualTolerance = true
  ExtensionAngle = 0
  FormatSpec = %.2w
  FormatSpecOverTolerance = %+.2w
  FormatSpecUnderTolerance = %+.2w
  Inverted = false
  LineAngle = 0
  LockPosition = false
  MeasureType = 1
  OverTolerance = 0
  References2D = -> [ProjItem002]
  Rotation = 0
  Scale = 0.5
  ScaleType = 0
  TheoreticalExact = false
  Type = 2
  UnderTolerance = 0
  X = 65.9361
  Y = 36.75
FEATURE [TechDraw::DrawPage] Page002  label="Front_dwg_05-06"
  KeepUpdated = true
  NextBalloonIndex = 1
  ProjectionType = 0
  Scale = 0.5
  Template = -> Template002
  Views = -> [ProjGroup002,Dimension042,Dimension043,Dimension044,Dimension045,Dimension046,Dimension047,Dimension048,Dimension049,Dimension050,Dimension051,Dimension052]
FEATURE [Sketcher::SketchObject] Sketch041
  FullyConstrained = true
  MapMode = 5
  Support = -> [XY_Plane003]
  sketch-geometry (16):
    g0: LineSegment StartX=-27 StartY=170 StartZ=0 EndX=207 EndY=170 EndZ=0
    g1: LineSegment StartX=210 StartY=167 StartZ=0 EndX=210 EndY=-27 EndZ=0
    g2: LineSegment StartX=207 StartY=-30 StartZ=0 EndX=-27 EndY=-30 EndZ=0
    g3: LineSegment StartX=-30 StartY=-27 StartZ=0 EndX=-30 EndY=167 EndZ=0
    g4: LineSegment StartX=-25 StartY=25 StartZ=0 EndX=25 EndY=25 EndZ=0
    g5: LineSegment StartX=25 StartY=25 StartZ=0 EndX=25 EndY=-25 EndZ=0
    g6: LineSegment StartX=25 StartY=-25 StartZ=0 EndX=-25 EndY=-25 EndZ=0
    g7: LineSegment StartX=-25 StartY=-25 StartZ=0 EndX=-25 EndY=25 EndZ=0
    g8: LineSegment StartX=155 StartY=165 StartZ=0 EndX=205 EndY=165 EndZ=0
    g9: LineSegment StartX=205 StartY=165 StartZ=0 EndX=205 EndY=115 EndZ=0
    g10: LineSegment StartX=205 StartY=115 StartZ=0 EndX=155 EndY=115 EndZ=0
    g11: LineSegment StartX=155 StartY=115 StartZ=0 EndX=155 EndY=165 EndZ=0
    g12: ArcOfCircle CenterX=-27 CenterY=-27 CenterZ=0 NormalX=0 NormalY=0 NormalZ=1 AngleXU=0 Radius=3 StartAngle=3.14159 EndAngle=4.71239
    g13: ArcOfCircle CenterX=207 CenterY=-27 CenterZ=0 NormalX=0 NormalY=0 NormalZ=1 AngleXU=0 Radius=3 StartAngle=4.71239 EndAngle=6.28319
    g14: ArcOfCircle CenterX=207 CenterY=167 CenterZ=0 NormalX=0 NormalY=0 NormalZ=1 AngleXU=0 Radius=3 StartAngle=1.7e-15 EndAngle=1.5708
    g15: ArcOfCircle CenterX=-27 CenterY=167 CenterZ=0 NormalX=0 NormalY=0 NormalZ=1 AngleXU=0 Radius=3 StartAngle=1.5708 EndAngle=3.14159
  constraints (44):
    c: Horizontal(g0)
    c: Horizontal(g2)
    c: Vertical(g1)
    c: Vertical(g3)
    c: Coincident(g4,g5)
    c: Coincident(g5,g6)
    c: Coincident(g6,g7)
    c: Coincident(g7,g4)
    c: Horizontal(g4)
    c: Horizontal(g6)
    c: Vertical(g5)
    c: Vertical(g7)
    c: DistanceY(g7,g7) = 50
    c: Coincident(g8,g9)
    c: Coincident(g9,g10)
    c: Coincident(g10,g11)
    c: Coincident(g11,g8)
    c: Horizontal(g8)
    c: Horizontal(g10)
    c: Vertical(g9)
    c: Vertical(g11)
    c: DistanceY(g9,g9) = 50
    c: DistanceX(g10,g10) = 50
    c: Distance(g9,g1) = 5
    c: Distance(g4,g3) = 5
    c: Distance(g6,g2) = 5
    c: Distance(g8,g0) = 5
    c: DistanceX(g6,g6) = 50
    c: Tangent(g2,g12) = 1.5708
    c: Tangent(g3,g12) = 1.5708
    c: Radius(g12) = 3
    c: Distance(g2,g0) = 200
    c: Tangent(g2,g13) = 1.5708
    c: Tangent(g1,g13) = 1.5708
    c: Tangent(g0,g14) = 1.5708
    c: Tangent(g1,g14) = 1.5708
    c: Tangent(g0,g15) = 1.5708
    c: Tangent(g3,g15) = 1.5708
    c: Equal(g12,g15)
    c: Equal(g12,g14)
    c: Equal(g12,g13)
    c: Distance(g3,g-2) = 30
    c: Distance(g2,g-1) = 30
    c: Distance(g3,g1) = 240
FEATURE [PartDesign::Pad] Pad006
  Direction = (0,0,1)
  Length = 15
  Length2 = 10
  Profile = -> Sketch041
  ReferenceAxis = -> Sketch041 [N_Axis]
  Reversed = true
  Type = 0
FEATURE [Sketcher::SketchObject] Sketch042  label="Sketch_rails_short_004"
  ExternalGeometry = -> [Pad006]
  FullyConstrained = true
  MapMode = 5
  Placement = pos=(210,0,0) rot=(0.57735,0.57735,0.57735;2.0944rad)
  Support = -> [Pad006]
  sketch-geometry (6):
    g0: LineSegment StartX=17.6906 StartY=-15 StartZ=0 EndX=20 EndY=-11 EndZ=0
    g1: LineSegment StartX=20 StartY=-11 StartZ=0 EndX=22.3094 EndY=-15 EndZ=0
    g2: LineSegment StartX=22.3094 StartY=-15 StartZ=0 EndX=17.6906 EndY=-15 EndZ=0
    g3: LineSegment StartX=117.691 StartY=-15 StartZ=0 EndX=120 EndY=-11 EndZ=0
    g4: LineSegment StartX=120 StartY=-11 StartZ=0 EndX=122.309 EndY=-15 EndZ=0
    g5: LineSegment StartX=122.309 StartY=-15 StartZ=0 EndX=117.691 EndY=-15 EndZ=0
  constraints (18):
    c: PointOnObject(g0,g-4)
    c: Coincident(g1,g0)
    c: PointOnObject(g1,g-4)
    c: Coincident(g2,g1)
    c: Coincident(g2,g0)
    c: Distance(g0,g2) = 4
    c: Angle(g0,g-2) = 0.523599
    c: Angle(g-2,g1) = 0.523599
    c: Coincident(g4,g3)
    c: Coincident(g5,g4)
    c: Coincident(g5,g3)
    c: Distance(g3,g5) = 4
    c: Angle(g3,g-2) = 0.523599
    c: Angle(g-2,g4) = 0.523599
    c: PointOnObject(g3,g-4)
    c: PointOnObject(g4,g-4)
    c: Distance(g0,g3) = 100
    c: Distance(g0,g-3) = 50
FEATURE [PartDesign::Pocket] Pocket009
  BaseFeature = -> Pad006
  Direction = (-1,0,0)
  Length = 5
  Length2 = 5
  Profile = -> Sketch042
  ReferenceAxis = -> Sketch042 [N_Axis]
  Type = 1
FEATURE [Sketcher::SketchObject] Sketch043  label="Sketch_rails_long_004"
  ExternalGeometry = -> [Pocket009]
  FullyConstrained = true
  MapMode = 5
  Placement = pos=(0,-30,0) rot=(1,0,0;1.5708rad)
  Support = -> [Pocket009]
  sketch-geometry (7):
    g0: LineSegment StartX=12.6906 StartY=-15 StartZ=0 EndX=15 EndY=-11 EndZ=0
    g1: LineSegment StartX=15 StartY=-11 StartZ=0 EndX=17.3094 EndY=-15 EndZ=0
    g2: LineSegment StartX=17.3094 StartY=-15 StartZ=0 EndX=12.6906 EndY=-15 EndZ=0
    g3: LineSegment StartX=162.691 StartY=-15 StartZ=0 EndX=165 EndY=-11 EndZ=0
    g4: LineSegment StartX=165 StartY=-11 StartZ=0 EndX=167.309 EndY=-15 EndZ=0
    g5: LineSegment StartX=167.309 StartY=-15 StartZ=0 EndX=162.691 EndY=-15 EndZ=0
    g6: LineSegment StartX=-30 StartY=-11 StartZ=0 EndX=210 EndY=-11 EndZ=0
  constraints (22):
    c: PointOnObject(g0,g-4)
    c: Coincident(g1,g0)
    c: PointOnObject(g1,g-4)
    c: Coincident(g2,g0)
    c: PointOnObject(g3,g-4)
    c: PointOnObject(g4,g-4)
    c: Coincident(g5,g3)
    c: Horizontal(g6)
    c: Distance(g-4,g6) = 4
    c: PointOnObject(g0,g6)
    c: PointOnObject(g3,g6)
    c: Coincident(g4,g3)
    c: DistanceX(g6,g6) = 240
    c: PointOnObject(g6,g-3)
    c: Angle(g0,g-2) = 0.523599
    c: Angle(g-2,g1) = 0.523599
    c: Angle(g3,g-2) = 0.523599
    c: Angle(g-2,g4) = 0.523599
    c: Coincident(g2,g1)
    c: Coincident(g5,g4)
    c: Distance(g0,g3) = 150
    c: Distance(g0,g-3) = 45
FEATURE [PartDesign::Pocket] Pocket010
  BaseFeature = -> Pocket009
  Direction = (0,1,-2e-16)
  Length = 5
  Length2 = 5
  Profile = -> Sketch043
  ReferenceAxis = -> Sketch043 [N_Axis]
  Type = 1
FEATURE [Sketcher::SketchObject] Sketch044
  ExternalGeometry = -> [Pocket010]
  FullyConstrained = false
  MapMode = 5
  Support = -> [Pocket010]
  sketch-geometry (42):
    g0: LineSegment StartX=-18 StartY=18 StartZ=0 EndX=18 EndY=18 EndZ=0
    g1: LineSegment StartX=18 StartY=18 StartZ=0 EndX=18 EndY=-18 EndZ=0
    g2: LineSegment StartX=-18 StartY=-18 StartZ=0 EndX=-18 EndY=18 EndZ=0
    g3: LineSegment StartX=180 StartY=170 StartZ=0 EndX=180 EndY=-30 EndZ=0
    g4: LineSegment StartX=-30 StartY=140 StartZ=0 EndX=210 EndY=140 EndZ=0
    g5: LineSegment StartX=162 StartY=158 StartZ=0 EndX=198 EndY=158 EndZ=0
    g6: LineSegment StartX=198 StartY=158 StartZ=0 EndX=198 EndY=122 EndZ=0
    g7: LineSegment StartX=198 StartY=122 StartZ=0 EndX=162 EndY=122 EndZ=0
    g8: LineSegment StartX=162 StartY=122 StartZ=0 EndX=162 EndY=158 EndZ=0
    g9: LineSegment StartX=-18 StartY=-18 StartZ=0 EndX=18 EndY=-18 EndZ=0
    g10: LineSegment StartX=-1e-16 StartY=-6 StartZ=0 EndX=-12 EndY=-6 EndZ=0
    g11: LineSegment StartX=-12 StartY=-6 StartZ=0 EndX=-12 EndY=0 EndZ=0
    g12: LineSegment StartX=-12 StartY=0 StartZ=0 EndX=-6 EndY=0 EndZ=0
    g13: LineSegment StartX=-6 StartY=0 StartZ=0 EndX=-6 EndY=6 EndZ=0
    g14: LineSegment StartX=-6 StartY=6 StartZ=0 EndX=-12 EndY=6 EndZ=0
    g15: LineSegment StartX=-12 StartY=6 StartZ=0 EndX=-12 EndY=12 EndZ=0
    g16: LineSegment StartX=-12 StartY=12 StartZ=0 EndX=0 EndY=12 EndZ=0
    g17: LineSegment StartX=0 StartY=12 StartZ=0 EndX=0 EndY=0 EndZ=0
    g18: LineSegment StartX=0 StartY=0 StartZ=0 EndX=12 EndY=2e-16 EndZ=0
    g19: LineSegment StartX=12 StartY=2e-16 StartZ=0 EndX=12 EndY=-6 EndZ=0
    g20: LineSegment StartX=12 StartY=-6 StartZ=0 EndX=6 EndY=-6 EndZ=0
    g21: LineSegment StartX=6 StartY=-6 StartZ=0 EndX=6 EndY=-12 EndZ=0
    g22: LineSegment StartX=6 StartY=-12 StartZ=0 EndX=0 EndY=-12 EndZ=0
    g23: LineSegment StartX=0 StartY=-12 StartZ=0 EndX=-1e-16 EndY=-6 EndZ=0
    g24: LineSegment StartX=168 StartY=128 StartZ=0 EndX=168 EndY=152 EndZ=0
    g25: LineSegment StartX=168 StartY=152 StartZ=0 EndX=192 EndY=152 EndZ=0
    g26: LineSegment StartX=192 StartY=152 StartZ=0 EndX=192 EndY=146 EndZ=0
    g27: LineSegment StartX=192 StartY=146 StartZ=0 EndX=186 EndY=146 EndZ=0
    g28: LineSegment StartX=186 StartY=146 StartZ=0 EndX=186 EndY=140 EndZ=0
    g29: LineSegment StartX=186 StartY=140 StartZ=0 EndX=192 EndY=140 EndZ=0
    g30: LineSegment StartX=192 StartY=140 StartZ=0 EndX=192 EndY=134 EndZ=0
    g31: LineSegment StartX=192 StartY=134 StartZ=0 EndX=186 EndY=134 EndZ=0
    g32: LineSegment StartX=186 StartY=134 StartZ=0 EndX=186 EndY=140 EndZ=0
    g33: LineSegment StartX=186 StartY=140 StartZ=0 EndX=180 EndY=140 EndZ=0
    g34: LineSegment StartX=180 StartY=140 StartZ=0 EndX=180 EndY=134 EndZ=0
    g35: LineSegment StartX=180 StartY=134 StartZ=0 EndX=186 EndY=134 EndZ=0
    g36: LineSegment StartX=186 StartY=134 StartZ=0 EndX=186 EndY=128 EndZ=0
    g37: LineSegment StartX=186 StartY=128 StartZ=0 EndX=180 EndY=128 EndZ=0
    g38: LineSegment StartX=180 StartY=128 StartZ=0 EndX=180 EndY=134 EndZ=0
    g39: LineSegment StartX=180 StartY=134 StartZ=0 EndX=174 EndY=134 EndZ=0
    g40: LineSegment StartX=174 StartY=134 StartZ=0 EndX=174 EndY=128 EndZ=0
    g41: LineSegment StartX=174 StartY=128 StartZ=0 EndX=168 EndY=128 EndZ=0
  constraints (113):
    c: Coincident(g0,g1)
    c: Coincident(g2,g0)
    c: Horizontal(g0)
    c: Vertical(g1)
    c: DistanceX(g2,g1) = 36
    c: Symmetric(g2,g1,g-2)
    c: Symmetric(g0,g2,g-1)
    c: Vertical(g3)
    c: Horizontal(g4)
    c: PointOnObject(g3,g-4)
    c: PointOnObject(g4,g-5)
    c: PointOnObject(g4,g-3)
    c: Distance(g4,g-1) = 140
    c: Distance(g3,g-2) = 180
    c: Coincident(g5,g6)
    c: Coincident(g6,g7)
    c: Coincident(g7,g8)
    c: Coincident(g8,g5)
    c: Horizontal(g5)
    c: Horizontal(g7)
    c: Vertical(g6)
    c: Vertical(g8)
    c: DistanceY(g6,g6) = 36
    c: Equal(g5,g6)
    c: Distance(g5,g4) = 18
    c: Distance(g5,g3) = 18
    c: Coincident(g9,g2)
    c: Coincident(g9,g1)
    c: Equal(g2,g8)
    c: Horizontal(g10)
    c: Coincident(g10,g11)
    c: Vertical(g11)
    c: Coincident(g11,g12)
    c: Horizontal(g12)
    c: Coincident(g12,g13)
    c: Coincident(g13,g14)
    c: Horizontal(g14)
    c: Coincident(g14,g15)
    c: Coincident(g15,g16)
    c: Horizontal(g16)
    c: Coincident(g16,g17)
    c: Vertical(g17)
    c: Coincident(g17,g18)
    c: Coincident(g18,g19)
    c: Vertical(g19)
    c: Coincident(g19,g20)
    c: Coincident(g20,g21)
    c: Coincident(g21,g22)
    c: Horizontal(g22)
    c: Coincident(g22,g23)
    c: Coincident(g23,g10)
    c: Tangent(g17,g23)
    c: Tangent(g12,g18)
    c: Vertical(g21)
    c: Vertical(g13)
    c: Tangent(g10,g20)
    c: DistanceX(g22,g22) = 6
    c: DistanceX(g12,g12) = 6
    c: Distance(g12,g23) = 6
    c: Distance(g10,g2) = 6
    c: DistanceX(g20,g20) = 6
    c: DistanceY(g11,g11) = 6
    c: DistanceY(g15,g15) = 6
    c: DistanceY(g13,g13) = 6
    c: Distance(g22,g9) = 6
    c: DistanceY(g23,g23) = 6
    c: Tangent(g15,g11)
    c: Vertical(g24)
    c: Coincident(g24,g25)
    c: Horizontal(g25)
    c: Coincident(g25,g26)
    c: Vertical(g26)
    c: Coincident(g26,g27)
    c: Horizontal(g27)
    c: Coincident(g27,g28)
    c: Vertical(g28)
    c: Coincident(g28,g29)
    c: Horizontal(g29)
    c: Coincident(g29,g30)
    c: Coincident(g30,g31)
    c: Horizontal(g31)
    c: Coincident(g31,g32)
    c: Coincident(g32,g33)
    c: Coincident(g33,g34)
    c: Vertical(g34)
    c: Coincident(g34,g35)
    c: Coincident(g35,g36)
    c: Coincident(g36,g37)
    c: Horizontal(g37)
    c: Coincident(g37,g38)
    c: Coincident(g38,g39)
    c: Coincident(g39,g40)
    c: Vertical(g40)
    c: Coincident(g40,g41)
    c: Coincident(g41,g24)
    c: Tangent(g41,g37)
    c: Tangent(g39,g35)
    c: Tangent(g35,g31)
    c: Tangent(g33,g29)
    c: Tangent(g38,g34)
    c: Tangent(g36,g32)
    c: Tangent(g32,g28)
    c: Distance(g25,g5) = 6
    c: Distance(g25,g6) = 6
    c: Tangent(g26,g30)
    c: DistanceY(g26,g26) = 6
    c: DistanceY(g28,g28) = 6
    c: DistanceY(g30,g30) = 6
    c: DistanceY(g36,g36) = 6
    c: DistanceX(g27,g27) = 6
    c: DistanceX(g33,g33) = 6
    c: DistanceX(g39,g39) = 6
    c: DistanceX(g41,g41) = 6
FEATURE [PartDesign::Pad] Pad007
  BaseFeature = -> Pocket010
  Direction = (0,0,1)
  Length = 1.2
  Length2 = 10
  Midplane = true
  Profile = -> Sketch044
  ReferenceAxis = -> Sketch044 [N_Axis]
  Type = 0
FEATURE [Sketcher::SketchObject] Sketch045
  FullyConstrained = true
  MapMode = 5
  Support = -> [Pad007]
  sketch-geometry (4):
    g0: Circle CenterX=20 CenterY=80 CenterZ=0 NormalX=0 NormalY=0 NormalZ=1 AngleXU=0 Radius=8
    g1: Circle CenterX=120 CenterY=140 CenterZ=0 NormalX=0 NormalY=0 NormalZ=1 AngleXU=0 Radius=8
    g2: Circle CenterX=180 CenterY=0 CenterZ=0 NormalX=0 NormalY=0 NormalZ=1 AngleXU=0 Radius=8
    g3: Circle CenterX=80 CenterY=0 CenterZ=0 NormalX=0 NormalY=0 NormalZ=1 AngleXU=0 Radius=8
  constraints (12):
    c: Diameter(g0) = 16
    c: Distance(g2,g-2) = 180
    c: Equal(g2,g0)
    c: Distance(g3,g-2) = 80
    c: Equal(g3,g0)
    c: Distance(g1,g-2) = 120
    c: Distance(g1,g-1) = 140
    c: Equal(g0,g1)
    c: Distance(g0,g-1) = 80
    c: PointOnObject(g3,g-1)
    c: PointOnObject(g2,g-1)
    c: Distance(g0,g-2) = 20
FEATURE [PartDesign::Pocket] Pocket011
  BaseFeature = -> Pad007
  Direction = (0,0,-1)
  Length = 5
  Length2 = 5
  Profile = -> Sketch045
  ReferenceAxis = -> Sketch045 [N_Axis]
  Type = 1
FEATURE [PartDesign::Plane] DatumPlane003
  AttachmentOffset = pos=(0,0,-10) rot=(0,0,1;0rad)
  Length = 60
  MapMode = 5
  Placement = pos=(0,0,-10) rot=(0,0,1;0rad)
  ResizeMode = 0
  Support = -> [Pocket011]
  Width = 60
FEATURE [Sketcher::SketchObject] Sketch046
  ExternalGeometry = -> [Pocket011]
  FullyConstrained = true
  MapMode = 5
  Support = -> [Pocket011]
  sketch-geometry (4):
    g0: LineSegment StartX=58 StartY=22 StartZ=0 EndX=102 EndY=22 EndZ=0
    g1: LineSegment StartX=102 StartY=22 StartZ=0 EndX=102 EndY=-22 EndZ=0
    g2: LineSegment StartX=102 StartY=-22 StartZ=0 EndX=58 EndY=-22 EndZ=0
    g3: LineSegment StartX=58 StartY=-22 StartZ=0 EndX=58 EndY=22 EndZ=0
  constraints (11):
    c: Coincident(g0,g1)
    c: Coincident(g1,g2)
    c: Coincident(g2,g3)
    c: Coincident(g3,g0)
    c: Horizontal(g0)
    c: Horizontal(g2)
    c: Vertical(g1)
    c: Vertical(g3)
    c: DistanceY(g3,g3) = 44
    c: Equal(g3,g0)
    c: Symmetric(g0,g1,g-3)
FEATURE [Sketcher::SketchObject] Sketch047
  ExternalGeometry = -> [Pocket011]
  FullyConstrained = true
  MapMode = 5
  Placement = pos=(0,0,-10) rot=(0,0,1;0rad)
  Support = -> [DatumPlane003]
  sketch-geometry (4):
    g0: LineSegment StartX=60.5 StartY=19.5 StartZ=0 EndX=99.5 EndY=19.5 EndZ=0
    g1: LineSegment StartX=99.5 StartY=19.5 StartZ=0 EndX=99.5 EndY=-19.5 EndZ=0
    g2: LineSegment StartX=99.5 StartY=-19.5 StartZ=0 EndX=60.5 EndY=-19.5 EndZ=0
    g3: LineSegment StartX=60.5 StartY=-19.5 StartZ=0 EndX=60.5 EndY=19.5 EndZ=0
  constraints (11):
    c: Coincident(g0,g1)
    c: Coincident(g1,g2)
    c: Coincident(g2,g3)
    c: Coincident(g3,g0)
    c: Horizontal(g0)
    c: Horizontal(g2)
    c: Vertical(g1)
    c: Vertical(g3)
    c: DistanceY(g3,g3) = 39
    c: Equal(g3,g0)
    c: Symmetric(g0,g1,g-3)
FEATURE [Sketcher::SketchObject] Sketch048
  ExternalGeometry = -> [Pocket011]
  FullyConstrained = true
  MapMode = 5
  Support = -> [Pocket011]
  sketch-geometry (4):
    g0: LineSegment StartX=98 StartY=162 StartZ=0 EndX=142 EndY=162 EndZ=0
    g1: LineSegment StartX=142 StartY=162 StartZ=0 EndX=142 EndY=118 EndZ=0
    g2: LineSegment StartX=142 StartY=118 StartZ=0 EndX=98 EndY=118 EndZ=0
    g3: LineSegment StartX=98 StartY=118 StartZ=0 EndX=98 EndY=162 EndZ=0
  constraints (11):
    c: Coincident(g0,g1)
    c: Coincident(g1,g2)
    c: Coincident(g2,g3)
    c: Coincident(g3,g0)
    c: Horizontal(g0)
    c: Horizontal(g2)
    c: Vertical(g1)
    c: Vertical(g3)
    c: DistanceY(g3,g3) = 44
    c: Equal(g3,g0)
    c: Symmetric(g0,g1,g-3)
FEATURE [Sketcher::SketchObject] Sketch049
  ExternalGeometry = -> [Pocket011]
  FullyConstrained = true
  MapMode = 5
  Placement = pos=(0,0,-10) rot=(0,0,1;0rad)
  Support = -> [DatumPlane003]
  sketch-geometry (4):
    g0: LineSegment StartX=139.5 StartY=159.5 StartZ=0 EndX=100.5 EndY=159.5 EndZ=0
    g1: LineSegment StartX=100.5 StartY=159.5 StartZ=0 EndX=100.5 EndY=120.5 EndZ=0
    g2: LineSegment StartX=100.5 StartY=120.5 StartZ=0 EndX=139.5 EndY=120.5 EndZ=0
    g3: LineSegment StartX=139.5 StartY=120.5 StartZ=0 EndX=139.5 EndY=159.5 EndZ=0
  constraints (11):
    c: Coincident(g0,g1)
    c: Coincident(g1,g2)
    c: Coincident(g2,g3)
    c: Coincident(g3,g0)
    c: Horizontal(g0)
    c: Horizontal(g2)
    c: Vertical(g1)
    c: Vertical(g3)
    c: DistanceY(g3,g3) = 39
    c: Equal(g3,g0)
    c: Symmetric(g0,g1,g-3)
FEATURE [Sketcher::SketchObject] Sketch052
  ExternalGeometry = -> [Pocket011]
  FullyConstrained = true
  MapMode = 5
  Support = -> [Pocket011]
  sketch-geometry (4):
    g0: LineSegment StartX=-2 StartY=102 StartZ=0 EndX=42 EndY=102 EndZ=0
    g1: LineSegment StartX=42 StartY=102 StartZ=0 EndX=42 EndY=58 EndZ=0
    g2: LineSegment StartX=42 StartY=58 StartZ=0 EndX=-2 EndY=58 EndZ=0
    g3: LineSegment StartX=-2 StartY=58 StartZ=0 EndX=-2 EndY=102 EndZ=0
  constraints (11):
    c: Coincident(g0,g1)
    c: Coincident(g1,g2)
    c: Coincident(g2,g3)
    c: Coincident(g3,g0)
    c: Horizontal(g0)
    c: Horizontal(g2)
    c: Vertical(g1)
    c: Vertical(g3)
    c: DistanceY(g3,g3) = 44
    c: Equal(g3,g0)
    c: Symmetric(g0,g1,g-3)
FEATURE [Sketcher::SketchObject] Sketch053
  ExternalGeometry = -> [Pocket011]
  FullyConstrained = true
  MapMode = 5
  Placement = pos=(0,0,-10) rot=(0,0,1;0rad)
  Support = -> [DatumPlane003]
  sketch-geometry (4):
    g0: LineSegment StartX=39.5 StartY=99.5 StartZ=0 EndX=0.5 EndY=99.5 EndZ=0
    g1: LineSegment StartX=0.5 StartY=99.5 StartZ=0 EndX=0.5 EndY=60.5 EndZ=0
    g2: LineSegment StartX=0.5 StartY=60.5 StartZ=0 EndX=39.5 EndY=60.5 EndZ=0
    g3: LineSegment StartX=39.5 StartY=60.5 StartZ=0 EndX=39.5 EndY=99.5 EndZ=0
  constraints (11):
    c: Coincident(g0,g1)
    c: Coincident(g1,g2)
    c: Coincident(g2,g3)
    c: Coincident(g3,g0)
    c: Horizontal(g0)
    c: Horizontal(g2)
    c: Vertical(g1)
    c: Vertical(g3)
    c: DistanceY(g3,g3) = 39
    c: Equal(g0,g3)
    c: Symmetric(g0,g1,g-3)
FEATURE [PartDesign::SubtractiveLoft] SubtractiveLoft012
  BaseFeature = -> Pocket011
  Closed = false
  Profile = -> Sketch053
  Ruled = false
  Sections = -> [Sketch052]
FEATURE [PartDesign::SubtractiveLoft] SubtractiveLoft013
  BaseFeature = -> SubtractiveLoft012
  Closed = false
  Profile = -> Sketch046
  Ruled = false
  Sections = -> [Sketch047]
FEATURE [PartDesign::SubtractiveLoft] SubtractiveLoft014
  BaseFeature = -> SubtractiveLoft013
  Closed = false
  Profile = -> Sketch048
  Ruled = false
  Sections = -> [Sketch049]
FEATURE [Sketcher::SketchObject] Sketch050
  ExternalGeometry = -> [SubtractiveLoft014]
  FullyConstrained = true
  MapMode = 5
  Support = -> [SubtractiveLoft014]
  sketch-geometry (4):
    g0: LineSegment StartX=158 StartY=22 StartZ=0 EndX=202 EndY=22 EndZ=0
    g1: LineSegment StartX=202 StartY=22 StartZ=0 EndX=202 EndY=-22 EndZ=0
    g2: LineSegment StartX=202 StartY=-22 StartZ=0 EndX=158 EndY=-22 EndZ=0
    g3: LineSegment StartX=158 StartY=-22 StartZ=0 EndX=158 EndY=22 EndZ=0
  constraints (11):
    c: Coincident(g0,g1)
    c: Coincident(g1,g2)
    c: Coincident(g2,g3)
    c: Coincident(g3,g0)
    c: Horizontal(g0)
    c: Horizontal(g2)
    c: Vertical(g1)
    c: Vertical(g3)
    c: DistanceY(g3,g3) = 44
    c: Equal(g3,g0)
    c: Symmetric(g0,g1,g-3)
FEATURE [Sketcher::SketchObject] Sketch051
  ExternalGeometry = -> [SubtractiveLoft014]
  FullyConstrained = true
  MapMode = 5
  Placement = pos=(0,0,-10) rot=(0,0,1;0rad)
  Support = -> [DatumPlane003]
  sketch-geometry (4):
    g0: LineSegment StartX=160.5 StartY=19.5 StartZ=0 EndX=199.5 EndY=19.5 EndZ=0
    g1: LineSegment StartX=199.5 StartY=19.5 StartZ=0 EndX=199.5 EndY=-19.5 EndZ=0
    g2: LineSegment StartX=199.5 StartY=-19.5 StartZ=0 EndX=160.5 EndY=-19.5 EndZ=0
    g3: LineSegment StartX=160.5 StartY=-19.5 StartZ=0 EndX=160.5 EndY=19.5 EndZ=0
  constraints (11):
    c: Coincident(g0,g1)
    c: Coincident(g1,g2)
    c: Coincident(g2,g3)
    c: Coincident(g3,g0)
    c: Horizontal(g0)
    c: Horizontal(g2)
    c: Vertical(g1)
    c: Vertical(g3)
    c: DistanceY(g3,g3) = 39
    c: Equal(g3,g0)
    c: Symmetric(g0,g1,g-3)
FEATURE [PartDesign::SubtractiveLoft] SubtractiveLoft015
  BaseFeature = -> SubtractiveLoft014
  Closed = false
  Profile = -> Sketch050
  Ruled = false
  Sections = -> [Sketch051]
FEATURE [PartDesign::Chamfer] Chamfer007
  Angle = 45
  Base = -> SubtractiveLoft015 [Edge32,Edge30,Edge31,Edge33,Edge24,Edge22,Edge25,Edge23,Edge27,Edge28,Edge29,Edge26,Edge37,Edge35,Edge34,Edge36]
  BaseFeature = -> SubtractiveLoft015
  ChamferType = 0
  FlipDirection = false
  Size = 1
  Size2 = 1
  SupportTransform = false
  UseAllEdges = false
FEATURE [PartDesign::Fillet] Fillet003
  Base = -> Chamfer007 [Edge9]
  BaseFeature = -> Chamfer007
  Radius = 1
  SupportTransform = false
  UseAllEdges = false
FEATURE [PartDesign::Chamfer] Chamfer008
  Angle = 45
  Base = -> Fillet003 [Edge98,Edge121,Edge109,Edge104,Edge101,Edge106,Edge110,Edge124,Edge116,Edge135,Edge132,Edge119,Edge130,Edge113,Edge126,Edge129]
  BaseFeature = -> Fillet003
  ChamferType = 0
  FlipDirection = false
  Size = 0.6
  Size2 = 1
  SupportTransform = false
  UseAllEdges = false
FEATURE [PartDesign::Chamfer] Chamfer009
  Angle = 45
  Base = -> Chamfer008 [Edge54,Edge209,Edge290,Edge289,Edge278,Edge371,Edge301,Edge363,Edge122,Edge299]
  BaseFeature = -> Chamfer008
  ChamferType = 0
  FlipDirection = false
  Size = 0.6
  Size2 = 1
  SupportTransform = false
  UseAllEdges = false
FEATURE [PartDesign::Body] Body003  label="Main_desk_07-08"
  Group = -> [Sketch041,Pad006,Sketch042,Pocket009,Sketch043,Pocket010,Sketch044,Pad007,Sketch045,Pocket011,DatumPlane003,Sketch046,Sketch047,Sketch048,Sketch049,Sketch050,Sketch051,Sketch052,Sketch053,SubtractiveLoft012,SubtractiveLoft013,SubtractiveLoft014,SubtractiveLoft015,Chamfer007,Fillet003,Chamfer008,Chamfer009]
  Origin = -> Origin003
  Tip = -> Chamfer009
FEATURE [TechDraw::DrawSVGTemplate] Template003
  Height = 297
  Orientation = 0
  Template = C:/Program Files/FreeCAD 0.21/data/Mod/TechDraw/Templates/A4_Portrait_blank.svg
  Width = 210
FEATURE [TechDraw::DrawProjGroupItem] ProjItem003  label="Front003"
  CoarseView = false
  Direction = (0,0,1)
  Focus = 100
  HardHidden = false
  IsoCount = 0
  IsoHidden = false
  IsoVisible = false
  LockPosition = true
  Perspective = false
  Rotation = 0
  RotationVector = (1,0,0)
  ScaleType = 2
  ScrubCount = 0
  SeamHidden = false
  SeamVisible = false
  SmoothHidden = false
  SmoothVisible = true
  Source = -> [Body003]
  Type = 0
  X = 0
  XDirection = (1,0,0)
  Y = 0
FEATURE [TechDraw::DrawProjGroup] ProjGroup003
  Anchor = -> ProjItem003
  AutoDistribute = true
  LockPosition = false
  ProjectionType = 0
  Rotation = 0
  Scale = 0.5
  ScaleType = 0
  Source = -> [Body003]
  Views = -> [ProjItem003]
  X = 115.337
  Y = 169.198
  spacingX = 15
  spacingY = 15
FEATURE [TechDraw::DrawGeomHatch] GeomHatch004  label="GeomHatch004FX10"
  FilePattern = C:/Program Files/FreeCAD 0.21/data/Mod/TechDraw/PAT/FCPAT.pat
  NamePattern = Diamond
  PatternOffset = (0,0,0)
  PatternRotation = 0
  ScalePattern = 1
  Source = -> ProjItem003 [Face10]
FEATURE [TechDraw::DrawGeomHatch] GeomHatch005  label="GeomHatch005FX11"
  FilePattern = C:/Program Files/FreeCAD 0.21/data/Mod/TechDraw/PAT/FCPAT.pat
  NamePattern = Diamond
  PatternOffset = (0,0,0)
  PatternRotation = 0
  ScalePattern = 1
  Source = -> ProjItem003 [Face11]
FEATURE [TechDraw::DrawGeomHatch] GeomHatch006  label="GeomHatch006FX61"
  FilePattern = C:/Program Files/FreeCAD 0.21/data/Mod/TechDraw/PAT/FCPAT.pat
  NamePattern = Diamond
  PatternOffset = (0,0,0)
  PatternRotation = 0
  ScalePattern = 1
  Source = -> ProjItem003 [Face61]
FEATURE [TechDraw::DrawViewDimension] Dimension053
  AngleOverride = false
  Arbitrary = false
  ArbitraryTolerances = false
  EqualTolerance = true
  ExtensionAngle = 0
  FormatSpec = %.2w
  FormatSpecOverTolerance = %+.2w
  FormatSpecUnderTolerance = %+.2w
  Inverted = false
  LineAngle = 0
  LockPosition = false
  MeasureType = 1
  OverTolerance = 0
  References2D = -> [ProjItem003]
  Rotation = 0
  Scale = 0.5
  ScaleType = 0
  TheoreticalExact = false
  Type = 1
  UnderTolerance = 0
  X = -25.6434
  Y = -52.49
FEATURE [TechDraw::DrawViewDimension] Dimension054
  AngleOverride = false
  Arbitrary = false
  ArbitraryTolerances = false
  EqualTolerance = true
  ExtensionAngle = 0
  FormatSpec = %.2w
  FormatSpecOverTolerance = %+.2w
  FormatSpecUnderTolerance = %+.2w
  Inverted = false
  LineAngle = 0
  LockPosition = false
  MeasureType = 1
  OverTolerance = 0
  References2D = -> [ProjItem003]
  Rotation = 0
  Scale = 0.5
  ScaleType = 0
  TheoreticalExact = false
  Type = 1
  UnderTolerance = 0
  X = -25.7556
  Y = -59.8678
FEATURE [TechDraw::DrawViewDimension] Dimension055
  AngleOverride = false
  Arbitrary = false
  ArbitraryTolerances = false
  EqualTolerance = true
  ExtensionAngle = 0
  FormatSpec = %.2w
  FormatSpecOverTolerance = %+.2w
  FormatSpecUnderTolerance = %+.2w
  Inverted = false
  LineAngle = 0
  LockPosition = false
  MeasureType = 1
  OverTolerance = 0
  References2D = -> [ProjItem003]
  Rotation = 0
  Scale = 0.5
  ScaleType = 0
  TheoreticalExact = false
  Type = 1
  UnderTolerance = 0
  X = -15.7556
  Y = -66.8678
FEATURE [TechDraw::DrawViewDimension] Dimension056
  AngleOverride = false
  Arbitrary = false
  ArbitraryTolerances = false
  EqualTolerance = true
  ExtensionAngle = 0
  FormatSpec = %.2w
  FormatSpecOverTolerance = %+.2w
  FormatSpecUnderTolerance = %+.2w
  Inverted = false
  LineAngle = 0
  LockPosition = false
  MeasureType = 1
  OverTolerance = 0
  References2D = -> [ProjItem003]
  Rotation = 0
  Scale = 0.5
  ScaleType = 0
  TheoreticalExact = false
  Type = 1
  UnderTolerance = 0
  X = -0.75561
  Y = -73.8678
FEATURE [TechDraw::DrawViewDimension] Dimension057
  AngleOverride = false
  Arbitrary = false
  ArbitraryTolerances = false
  EqualTolerance = true
  ExtensionAngle = 0
  FormatSpec = %.2w
  FormatSpecOverTolerance = %+.2w
  FormatSpecUnderTolerance = %+.2w
  Inverted = false
  LineAngle = 0
  LockPosition = false
  MeasureType = 1
  OverTolerance = 0
  References2D = -> [ProjItem003]
  Rotation = 0
  Scale = 0.5
  ScaleType = 0
  TheoreticalExact = false
  Type = 2
  UnderTolerance = 0
  X = -69.4196
  Y = -14.3834
FEATURE [TechDraw::DrawViewDimension] Dimension058
  AngleOverride = false
  Arbitrary = false
  ArbitraryTolerances = false
  EqualTolerance = true
  ExtensionAngle = 0
  FormatSpec = %.2w
  FormatSpecOverTolerance = %+.2w
  FormatSpecUnderTolerance = %+.2w
  Inverted = false
  LineAngle = 0
  LockPosition = false
  MeasureType = 1
  OverTolerance = 0
  References2D = -> [ProjItem003]
  Rotation = 0
  Scale = 0.5
  ScaleType = 0
  TheoreticalExact = false
  Type = 2
  UnderTolerance = 0
  X = -77.154
  Y = 3.63903
FEATURE [TechDraw::DrawViewDimension] Dimension059
  AngleOverride = false
  Arbitrary = false
  ArbitraryTolerances = false
  EqualTolerance = true
  ExtensionAngle = 0
  FormatSpec = %.2w
  FormatSpecOverTolerance = %+.2w
  FormatSpecUnderTolerance = %+.2w
  Inverted = false
  LineAngle = 0
  LockPosition = false
  MeasureType = 1
  OverTolerance = 0
  References2D = -> [ProjItem003]
  Rotation = 0
  Scale = 0.5
  ScaleType = 0
  TheoreticalExact = false
  Type = 2
  UnderTolerance = 0
  X = -84.9464
  Y = 4.01683
FEATURE [TechDraw::DrawViewDimension] Dimension060
  AngleOverride = false
  Arbitrary = false
  ArbitraryTolerances = false
  EqualTolerance = true
  ExtensionAngle = 0
  FormatSpec = %.2w
  FormatSpecOverTolerance = %+.2w
  FormatSpecUnderTolerance = %+.2w
  Inverted = false
  LineAngle = 0
  LockPosition = false
  MeasureType = 1
  OverTolerance = 0
  References2D = -> [ProjItem003]
  Rotation = 0
  Scale = 0.5
  ScaleType = 0
  TheoreticalExact = false
  Type = 1
  UnderTolerance = 0
  X = -0.377805
  Y = -82.2637
FEATURE [TechDraw::DrawViewDimension] Dimension061
  AngleOverride = false
  Arbitrary = false
  ArbitraryTolerances = false
  EqualTolerance = true
  ExtensionAngle = 0
  FormatSpec = %.2w
  FormatSpecOverTolerance = %+.2w
  FormatSpecUnderTolerance = %+.2w
  Inverted = false
  LineAngle = 0
  LockPosition = false
  MeasureType = 1
  OverTolerance = 0
  References2D = -> [ProjItem003]
  Rotation = 0
  Scale = 0.5
  ScaleType = 0
  TheoreticalExact = false
  Type = 2
  UnderTolerance = 0
  X = 65.3342
  Y = 36.3722
FEATURE [TechDraw::DrawViewDimension] Dimension062
  AngleOverride = false
  Arbitrary = false
  ArbitraryTolerances = false
  EqualTolerance = true
  ExtensionAngle = 0
  FormatSpec = %.2w
  FormatSpecOverTolerance = %+.2w
  FormatSpecUnderTolerance = %+.2w
  Inverted = false
  LineAngle = 0
  LockPosition = false
  MeasureType = 1
  OverTolerance = 0
  References2D = -> [ProjItem003]
  Rotation = 0
  Scale = 0.5
  ScaleType = 0
  TheoreticalExact = false
  Type = 1
  UnderTolerance = 0
  X = 45
  Y = 59.7288
FEATURE [TechDraw::DrawPage] Page003  label="Front_dwg_07-08"
  KeepUpdated = true
  NextBalloonIndex = 1
  ProjectionType = 0
  Scale = 0.5
  Template = -> Template003
  Views = -> [ProjGroup003,Dimension053,Dimension054,Dimension055,Dimension056,Dimension057,Dimension058,Dimension059,Dimension060,Dimension061,Dimension062]
